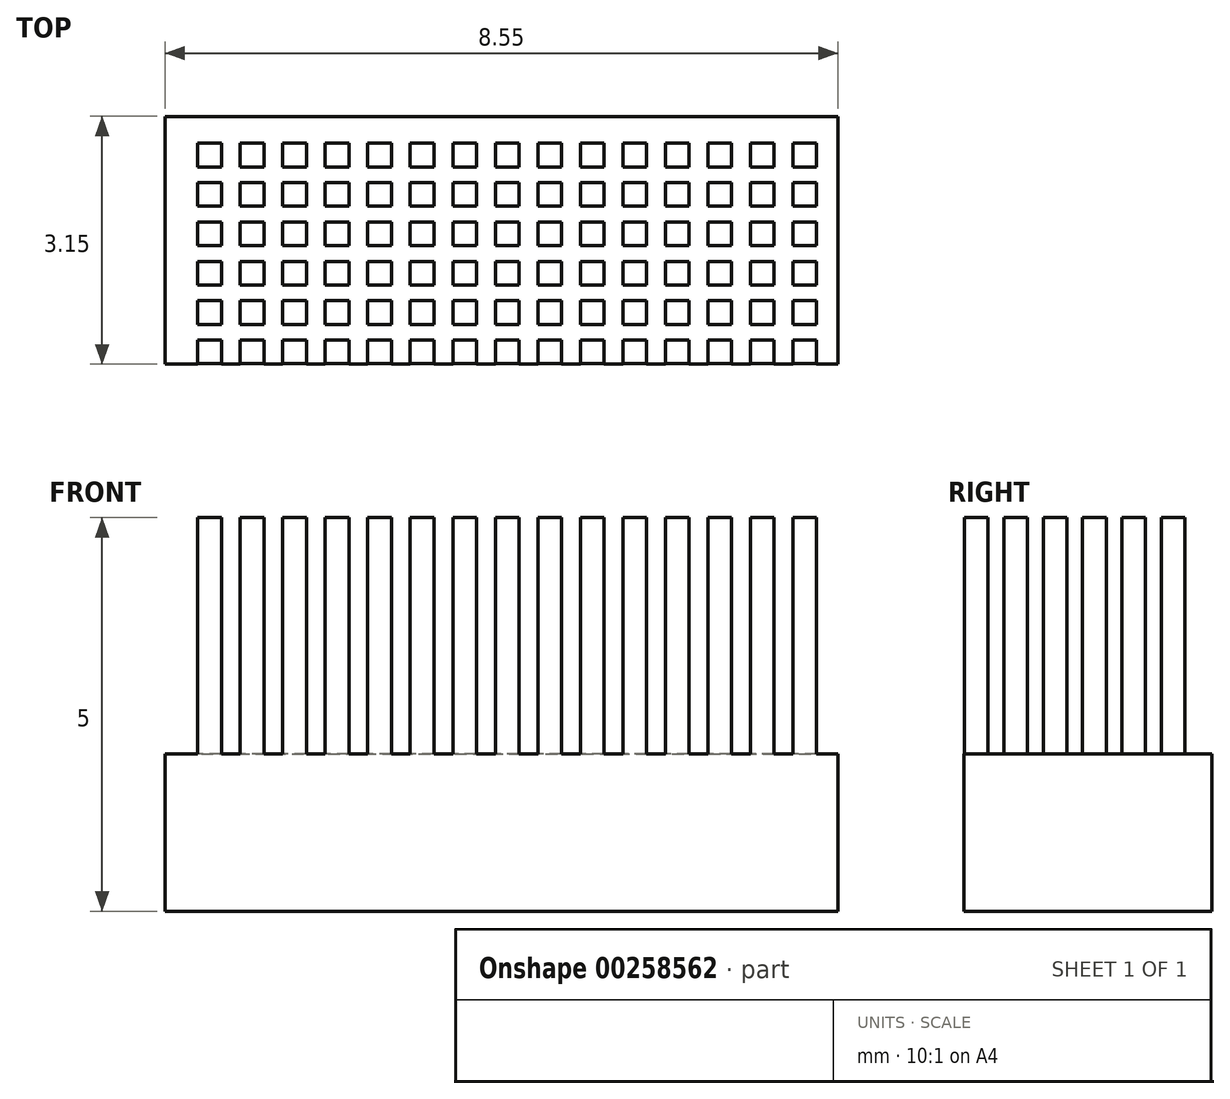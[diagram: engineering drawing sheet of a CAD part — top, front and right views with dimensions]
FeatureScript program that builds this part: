
annotation { "Feature Type Name" : "Feature", "Feature Type Description" : "" }
export const myFeature = defineFeature(function(context is Context, id is Id, definition is map)
    precondition{}
    {
        {
            var Q0;
            Q0=qCreatedBy(makeId("Top.planeOp"),FACE);
            var sketch = newSketch(context, id + "F0", { "sketchPlane" : qUnion([Q0])});
            skLineSegment(sketch, "E0.bottom", {"start": v(-12.29, 13.69) * mm, "end": v(-3.74, 13.69) * mm});
            skLineSegment(sketch, "E0.top", {"start": v(-12.29, 10.54) * mm, "end": v(-3.74, 10.54) * mm});
            skLineSegment(sketch, "E0.left", {"start": v(-12.29, 13.69) * mm, "end": v(-12.29, 10.54) * mm});
            skLineSegment(sketch, "E0.right", {"start": v(-3.74, 13.69) * mm, "end": v(-3.74, 10.54) * mm});
            skLineSegment(sketch, "E1.bottom", {"start": v(-11.87, 13.35) * mm, "end": v(-11.57, 13.35) * mm});
            skLineSegment(sketch, "E1.top", {"start": v(-11.87, 13.05) * mm, "end": v(-11.57, 13.05) * mm});
            skLineSegment(sketch, "E1.left", {"start": v(-11.87, 13.35) * mm, "end": v(-11.87, 13.05) * mm});
            skLineSegment(sketch, "E1.right", {"start": v(-11.57, 13.35) * mm, "end": v(-11.57, 13.05) * mm});
            skLineSegment(sketch, "E2.0.1.0", {"start": v(-11.87, 12.85) * mm, "end": v(-11.57, 12.85) * mm});
            skLineSegment(sketch, "E2.0.1.1", {"start": v(-11.57, 12.85) * mm, "end": v(-11.57, 12.55) * mm});
            skLineSegment(sketch, "E2.0.1.2", {"start": v(-11.87, 12.55) * mm, "end": v(-11.57, 12.55) * mm});
            skLineSegment(sketch, "E2.0.1.3", {"start": v(-11.87, 12.85) * mm, "end": v(-11.87, 12.55) * mm});
            skLineSegment(sketch, "E2.0.2.0", {"start": v(-11.87, 12.35) * mm, "end": v(-11.57, 12.35) * mm});
            skLineSegment(sketch, "E2.0.2.1", {"start": v(-11.57, 12.35) * mm, "end": v(-11.57, 12.05) * mm});
            skLineSegment(sketch, "E2.0.2.2", {"start": v(-11.87, 12.05) * mm, "end": v(-11.57, 12.05) * mm});
            skLineSegment(sketch, "E2.0.2.3", {"start": v(-11.87, 12.35) * mm, "end": v(-11.87, 12.05) * mm});
            skLineSegment(sketch, "E2.0.3.0", {"start": v(-11.87, 11.85) * mm, "end": v(-11.57, 11.85) * mm});
            skLineSegment(sketch, "E2.0.3.1", {"start": v(-11.57, 11.85) * mm, "end": v(-11.57, 11.55) * mm});
            skLineSegment(sketch, "E2.0.3.2", {"start": v(-11.87, 11.55) * mm, "end": v(-11.57, 11.55) * mm});
            skLineSegment(sketch, "E2.0.3.3", {"start": v(-11.87, 11.85) * mm, "end": v(-11.87, 11.55) * mm});
            skLineSegment(sketch, "E2.0.4.0", {"start": v(-11.87, 11.35) * mm, "end": v(-11.57, 11.35) * mm});
            skLineSegment(sketch, "E2.0.4.1", {"start": v(-11.57, 11.35) * mm, "end": v(-11.57, 11.05) * mm});
            skLineSegment(sketch, "E2.0.4.2", {"start": v(-11.87, 11.05) * mm, "end": v(-11.57, 11.05) * mm});
            skLineSegment(sketch, "E2.0.4.3", {"start": v(-11.87, 11.35) * mm, "end": v(-11.87, 11.05) * mm});
            skLineSegment(sketch, "E2.0.5.0", {"start": v(-11.87, 10.85) * mm, "end": v(-11.57, 10.85) * mm});
            skLineSegment(sketch, "E2.0.5.1", {"start": v(-11.57, 10.85) * mm, "end": v(-11.57, 10.55) * mm});
            skLineSegment(sketch, "E2.0.5.2", {"start": v(-11.87, 10.55) * mm, "end": v(-11.57, 10.55) * mm});
            skLineSegment(sketch, "E2.0.5.3", {"start": v(-11.87, 10.85) * mm, "end": v(-11.87, 10.55) * mm});
            skLineSegment(sketch, "E2.1.0.0", {"start": v(-11.33, 13.35) * mm, "end": v(-11.03, 13.35) * mm});
            skLineSegment(sketch, "E2.1.0.1", {"start": v(-11.03, 13.35) * mm, "end": v(-11.03, 13.05) * mm});
            skLineSegment(sketch, "E2.1.0.2", {"start": v(-11.33, 13.05) * mm, "end": v(-11.03, 13.05) * mm});
            skLineSegment(sketch, "E2.1.0.3", {"start": v(-11.33, 13.35) * mm, "end": v(-11.33, 13.05) * mm});
            skLineSegment(sketch, "E2.1.1.0", {"start": v(-11.33, 12.85) * mm, "end": v(-11.03, 12.85) * mm});
            skLineSegment(sketch, "E2.1.1.1", {"start": v(-11.03, 12.85) * mm, "end": v(-11.03, 12.55) * mm});
            skLineSegment(sketch, "E2.1.1.2", {"start": v(-11.33, 12.55) * mm, "end": v(-11.03, 12.55) * mm});
            skLineSegment(sketch, "E2.1.1.3", {"start": v(-11.33, 12.85) * mm, "end": v(-11.33, 12.55) * mm});
            skLineSegment(sketch, "E2.1.2.0", {"start": v(-11.33, 12.35) * mm, "end": v(-11.03, 12.35) * mm});
            skLineSegment(sketch, "E2.1.2.1", {"start": v(-11.03, 12.35) * mm, "end": v(-11.03, 12.05) * mm});
            skLineSegment(sketch, "E2.1.2.2", {"start": v(-11.33, 12.05) * mm, "end": v(-11.03, 12.05) * mm});
            skLineSegment(sketch, "E2.1.2.3", {"start": v(-11.33, 12.35) * mm, "end": v(-11.33, 12.05) * mm});
            skLineSegment(sketch, "E2.1.3.0", {"start": v(-11.33, 11.85) * mm, "end": v(-11.03, 11.85) * mm});
            skLineSegment(sketch, "E2.1.3.1", {"start": v(-11.03, 11.85) * mm, "end": v(-11.03, 11.55) * mm});
            skLineSegment(sketch, "E2.1.3.2", {"start": v(-11.33, 11.55) * mm, "end": v(-11.03, 11.55) * mm});
            skLineSegment(sketch, "E2.1.3.3", {"start": v(-11.33, 11.85) * mm, "end": v(-11.33, 11.55) * mm});
            skLineSegment(sketch, "E2.1.4.0", {"start": v(-11.33, 11.35) * mm, "end": v(-11.03, 11.35) * mm});
            skLineSegment(sketch, "E2.1.4.1", {"start": v(-11.03, 11.35) * mm, "end": v(-11.03, 11.05) * mm});
            skLineSegment(sketch, "E2.1.4.2", {"start": v(-11.33, 11.05) * mm, "end": v(-11.03, 11.05) * mm});
            skLineSegment(sketch, "E2.1.4.3", {"start": v(-11.33, 11.35) * mm, "end": v(-11.33, 11.05) * mm});
            skLineSegment(sketch, "E2.1.5.0", {"start": v(-11.33, 10.85) * mm, "end": v(-11.03, 10.85) * mm});
            skLineSegment(sketch, "E2.1.5.1", {"start": v(-11.03, 10.85) * mm, "end": v(-11.03, 10.55) * mm});
            skLineSegment(sketch, "E2.1.5.2", {"start": v(-11.33, 10.55) * mm, "end": v(-11.03, 10.55) * mm});
            skLineSegment(sketch, "E2.1.5.3", {"start": v(-11.33, 10.85) * mm, "end": v(-11.33, 10.55) * mm});
            skLineSegment(sketch, "E2.2.0.0", {"start": v(-10.8, 13.35) * mm, "end": v(-10.5, 13.35) * mm});
            skLineSegment(sketch, "E2.2.0.1", {"start": v(-10.5, 13.35) * mm, "end": v(-10.5, 13.05) * mm});
            skLineSegment(sketch, "E2.2.0.2", {"start": v(-10.8, 13.05) * mm, "end": v(-10.5, 13.05) * mm});
            skLineSegment(sketch, "E2.2.0.3", {"start": v(-10.8, 13.35) * mm, "end": v(-10.8, 13.05) * mm});
            skLineSegment(sketch, "E2.2.1.0", {"start": v(-10.8, 12.85) * mm, "end": v(-10.5, 12.85) * mm});
            skLineSegment(sketch, "E2.2.1.1", {"start": v(-10.5, 12.85) * mm, "end": v(-10.5, 12.55) * mm});
            skLineSegment(sketch, "E2.2.1.2", {"start": v(-10.8, 12.55) * mm, "end": v(-10.5, 12.55) * mm});
            skLineSegment(sketch, "E2.2.1.3", {"start": v(-10.8, 12.85) * mm, "end": v(-10.8, 12.55) * mm});
            skLineSegment(sketch, "E2.2.2.0", {"start": v(-10.8, 12.35) * mm, "end": v(-10.5, 12.35) * mm});
            skLineSegment(sketch, "E2.2.2.1", {"start": v(-10.5, 12.35) * mm, "end": v(-10.5, 12.05) * mm});
            skLineSegment(sketch, "E2.2.2.2", {"start": v(-10.8, 12.05) * mm, "end": v(-10.5, 12.05) * mm});
            skLineSegment(sketch, "E2.2.2.3", {"start": v(-10.8, 12.35) * mm, "end": v(-10.8, 12.05) * mm});
            skLineSegment(sketch, "E2.2.3.0", {"start": v(-10.8, 11.85) * mm, "end": v(-10.5, 11.85) * mm});
            skLineSegment(sketch, "E2.2.3.1", {"start": v(-10.5, 11.85) * mm, "end": v(-10.5, 11.55) * mm});
            skLineSegment(sketch, "E2.2.3.2", {"start": v(-10.8, 11.55) * mm, "end": v(-10.5, 11.55) * mm});
            skLineSegment(sketch, "E2.2.3.3", {"start": v(-10.8, 11.85) * mm, "end": v(-10.8, 11.55) * mm});
            skLineSegment(sketch, "E2.2.4.0", {"start": v(-10.8, 11.35) * mm, "end": v(-10.5, 11.35) * mm});
            skLineSegment(sketch, "E2.2.4.1", {"start": v(-10.5, 11.35) * mm, "end": v(-10.5, 11.05) * mm});
            skLineSegment(sketch, "E2.2.4.2", {"start": v(-10.8, 11.05) * mm, "end": v(-10.5, 11.05) * mm});
            skLineSegment(sketch, "E2.2.4.3", {"start": v(-10.8, 11.35) * mm, "end": v(-10.8, 11.05) * mm});
            skLineSegment(sketch, "E2.2.5.0", {"start": v(-10.8, 10.85) * mm, "end": v(-10.5, 10.85) * mm});
            skLineSegment(sketch, "E2.2.5.1", {"start": v(-10.5, 10.85) * mm, "end": v(-10.5, 10.55) * mm});
            skLineSegment(sketch, "E2.2.5.2", {"start": v(-10.8, 10.55) * mm, "end": v(-10.5, 10.55) * mm});
            skLineSegment(sketch, "E2.2.5.3", {"start": v(-10.8, 10.85) * mm, "end": v(-10.8, 10.55) * mm});
            skLineSegment(sketch, "E2.3.0.0", {"start": v(-10.25, 13.35) * mm, "end": v(-9.95, 13.35) * mm});
            skLineSegment(sketch, "E2.3.0.1", {"start": v(-9.95, 13.35) * mm, "end": v(-9.95, 13.05) * mm});
            skLineSegment(sketch, "E2.3.0.2", {"start": v(-10.25, 13.05) * mm, "end": v(-9.95, 13.05) * mm});
            skLineSegment(sketch, "E2.3.0.3", {"start": v(-10.25, 13.35) * mm, "end": v(-10.25, 13.05) * mm});
            skLineSegment(sketch, "E2.3.1.0", {"start": v(-10.25, 12.85) * mm, "end": v(-9.95, 12.85) * mm});
            skLineSegment(sketch, "E2.3.1.1", {"start": v(-9.95, 12.85) * mm, "end": v(-9.95, 12.55) * mm});
            skLineSegment(sketch, "E2.3.1.2", {"start": v(-10.25, 12.55) * mm, "end": v(-9.95, 12.55) * mm});
            skLineSegment(sketch, "E2.3.1.3", {"start": v(-10.25, 12.85) * mm, "end": v(-10.25, 12.55) * mm});
            skLineSegment(sketch, "E2.3.2.0", {"start": v(-10.25, 12.35) * mm, "end": v(-9.95, 12.35) * mm});
            skLineSegment(sketch, "E2.3.2.1", {"start": v(-9.95, 12.35) * mm, "end": v(-9.95, 12.05) * mm});
            skLineSegment(sketch, "E2.3.2.2", {"start": v(-10.25, 12.05) * mm, "end": v(-9.95, 12.05) * mm});
            skLineSegment(sketch, "E2.3.2.3", {"start": v(-10.25, 12.35) * mm, "end": v(-10.25, 12.05) * mm});
            skLineSegment(sketch, "E2.3.3.0", {"start": v(-10.25, 11.85) * mm, "end": v(-9.95, 11.85) * mm});
            skLineSegment(sketch, "E2.3.3.1", {"start": v(-9.95, 11.85) * mm, "end": v(-9.95, 11.55) * mm});
            skLineSegment(sketch, "E2.3.3.2", {"start": v(-10.25, 11.55) * mm, "end": v(-9.95, 11.55) * mm});
            skLineSegment(sketch, "E2.3.3.3", {"start": v(-10.25, 11.85) * mm, "end": v(-10.25, 11.55) * mm});
            skLineSegment(sketch, "E2.3.4.0", {"start": v(-10.25, 11.35) * mm, "end": v(-9.95, 11.35) * mm});
            skLineSegment(sketch, "E2.3.4.1", {"start": v(-9.95, 11.35) * mm, "end": v(-9.95, 11.05) * mm});
            skLineSegment(sketch, "E2.3.4.2", {"start": v(-10.25, 11.05) * mm, "end": v(-9.95, 11.05) * mm});
            skLineSegment(sketch, "E2.3.4.3", {"start": v(-10.25, 11.35) * mm, "end": v(-10.25, 11.05) * mm});
            skLineSegment(sketch, "E2.3.5.0", {"start": v(-10.25, 10.85) * mm, "end": v(-9.95, 10.85) * mm});
            skLineSegment(sketch, "E2.3.5.1", {"start": v(-9.95, 10.85) * mm, "end": v(-9.95, 10.55) * mm});
            skLineSegment(sketch, "E2.3.5.2", {"start": v(-10.25, 10.55) * mm, "end": v(-9.95, 10.55) * mm});
            skLineSegment(sketch, "E2.3.5.3", {"start": v(-10.25, 10.85) * mm, "end": v(-10.25, 10.55) * mm});
            skLineSegment(sketch, "E2.4.0.0", {"start": v(-9.71, 13.35) * mm, "end": v(-9.41, 13.35) * mm});
            skLineSegment(sketch, "E2.4.0.1", {"start": v(-9.41, 13.35) * mm, "end": v(-9.41, 13.05) * mm});
            skLineSegment(sketch, "E2.4.0.2", {"start": v(-9.71, 13.05) * mm, "end": v(-9.41, 13.05) * mm});
            skLineSegment(sketch, "E2.4.0.3", {"start": v(-9.71, 13.35) * mm, "end": v(-9.71, 13.05) * mm});
            skLineSegment(sketch, "E2.4.1.0", {"start": v(-9.71, 12.85) * mm, "end": v(-9.41, 12.85) * mm});
            skLineSegment(sketch, "E2.4.1.1", {"start": v(-9.41, 12.85) * mm, "end": v(-9.41, 12.55) * mm});
            skLineSegment(sketch, "E2.4.1.2", {"start": v(-9.71, 12.55) * mm, "end": v(-9.41, 12.55) * mm});
            skLineSegment(sketch, "E2.4.1.3", {"start": v(-9.71, 12.85) * mm, "end": v(-9.71, 12.55) * mm});
            skLineSegment(sketch, "E2.4.2.0", {"start": v(-9.71, 12.35) * mm, "end": v(-9.41, 12.35) * mm});
            skLineSegment(sketch, "E2.4.2.1", {"start": v(-9.41, 12.35) * mm, "end": v(-9.41, 12.05) * mm});
            skLineSegment(sketch, "E2.4.2.2", {"start": v(-9.71, 12.05) * mm, "end": v(-9.41, 12.05) * mm});
            skLineSegment(sketch, "E2.4.2.3", {"start": v(-9.71, 12.35) * mm, "end": v(-9.71, 12.05) * mm});
            skLineSegment(sketch, "E2.4.3.0", {"start": v(-9.71, 11.85) * mm, "end": v(-9.41, 11.85) * mm});
            skLineSegment(sketch, "E2.4.3.1", {"start": v(-9.41, 11.85) * mm, "end": v(-9.41, 11.55) * mm});
            skLineSegment(sketch, "E2.4.3.2", {"start": v(-9.71, 11.55) * mm, "end": v(-9.41, 11.55) * mm});
            skLineSegment(sketch, "E2.4.3.3", {"start": v(-9.71, 11.85) * mm, "end": v(-9.71, 11.55) * mm});
            skLineSegment(sketch, "E2.4.4.0", {"start": v(-9.71, 11.35) * mm, "end": v(-9.41, 11.35) * mm});
            skLineSegment(sketch, "E2.4.4.1", {"start": v(-9.41, 11.35) * mm, "end": v(-9.41, 11.05) * mm});
            skLineSegment(sketch, "E2.4.4.2", {"start": v(-9.71, 11.05) * mm, "end": v(-9.41, 11.05) * mm});
            skLineSegment(sketch, "E2.4.4.3", {"start": v(-9.71, 11.35) * mm, "end": v(-9.71, 11.05) * mm});
            skLineSegment(sketch, "E2.4.5.0", {"start": v(-9.71, 10.85) * mm, "end": v(-9.41, 10.85) * mm});
            skLineSegment(sketch, "E2.4.5.1", {"start": v(-9.41, 10.85) * mm, "end": v(-9.41, 10.55) * mm});
            skLineSegment(sketch, "E2.4.5.2", {"start": v(-9.71, 10.55) * mm, "end": v(-9.41, 10.55) * mm});
            skLineSegment(sketch, "E2.4.5.3", {"start": v(-9.71, 10.85) * mm, "end": v(-9.71, 10.55) * mm});
            skLineSegment(sketch, "E2.5.0.0", {"start": v(-9.17, 13.35) * mm, "end": v(-8.87, 13.35) * mm});
            skLineSegment(sketch, "E2.5.0.1", {"start": v(-8.87, 13.35) * mm, "end": v(-8.87, 13.05) * mm});
            skLineSegment(sketch, "E2.5.0.2", {"start": v(-9.17, 13.05) * mm, "end": v(-8.87, 13.05) * mm});
            skLineSegment(sketch, "E2.5.0.3", {"start": v(-9.17, 13.35) * mm, "end": v(-9.17, 13.05) * mm});
            skLineSegment(sketch, "E2.5.1.0", {"start": v(-9.17, 12.85) * mm, "end": v(-8.87, 12.85) * mm});
            skLineSegment(sketch, "E2.5.1.1", {"start": v(-8.87, 12.85) * mm, "end": v(-8.87, 12.55) * mm});
            skLineSegment(sketch, "E2.5.1.2", {"start": v(-9.17, 12.55) * mm, "end": v(-8.87, 12.55) * mm});
            skLineSegment(sketch, "E2.5.1.3", {"start": v(-9.17, 12.85) * mm, "end": v(-9.17, 12.55) * mm});
            skLineSegment(sketch, "E2.5.2.0", {"start": v(-9.17, 12.35) * mm, "end": v(-8.87, 12.35) * mm});
            skLineSegment(sketch, "E2.5.2.1", {"start": v(-8.87, 12.35) * mm, "end": v(-8.87, 12.05) * mm});
            skLineSegment(sketch, "E2.5.2.2", {"start": v(-9.17, 12.05) * mm, "end": v(-8.87, 12.05) * mm});
            skLineSegment(sketch, "E2.5.2.3", {"start": v(-9.17, 12.35) * mm, "end": v(-9.17, 12.05) * mm});
            skLineSegment(sketch, "E2.5.3.0", {"start": v(-9.17, 11.85) * mm, "end": v(-8.87, 11.85) * mm});
            skLineSegment(sketch, "E2.5.3.1", {"start": v(-8.87, 11.85) * mm, "end": v(-8.87, 11.55) * mm});
            skLineSegment(sketch, "E2.5.3.2", {"start": v(-9.17, 11.55) * mm, "end": v(-8.87, 11.55) * mm});
            skLineSegment(sketch, "E2.5.3.3", {"start": v(-9.17, 11.85) * mm, "end": v(-9.17, 11.55) * mm});
            skLineSegment(sketch, "E2.5.4.0", {"start": v(-9.17, 11.35) * mm, "end": v(-8.87, 11.35) * mm});
            skLineSegment(sketch, "E2.5.4.1", {"start": v(-8.87, 11.35) * mm, "end": v(-8.87, 11.05) * mm});
            skLineSegment(sketch, "E2.5.4.2", {"start": v(-9.17, 11.05) * mm, "end": v(-8.87, 11.05) * mm});
            skLineSegment(sketch, "E2.5.4.3", {"start": v(-9.17, 11.35) * mm, "end": v(-9.17, 11.05) * mm});
            skLineSegment(sketch, "E2.5.5.0", {"start": v(-9.17, 10.85) * mm, "end": v(-8.87, 10.85) * mm});
            skLineSegment(sketch, "E2.5.5.1", {"start": v(-8.87, 10.85) * mm, "end": v(-8.87, 10.55) * mm});
            skLineSegment(sketch, "E2.5.5.2", {"start": v(-9.17, 10.55) * mm, "end": v(-8.87, 10.55) * mm});
            skLineSegment(sketch, "E2.5.5.3", {"start": v(-9.17, 10.85) * mm, "end": v(-9.17, 10.55) * mm});
            skLineSegment(sketch, "E2.6.0.0", {"start": v(-8.63, 13.35) * mm, "end": v(-8.33, 13.35) * mm});
            skLineSegment(sketch, "E2.6.0.1", {"start": v(-8.33, 13.35) * mm, "end": v(-8.33, 13.05) * mm});
            skLineSegment(sketch, "E2.6.0.2", {"start": v(-8.63, 13.05) * mm, "end": v(-8.33, 13.05) * mm});
            skLineSegment(sketch, "E2.6.0.3", {"start": v(-8.63, 13.35) * mm, "end": v(-8.63, 13.05) * mm});
            skLineSegment(sketch, "E2.6.1.0", {"start": v(-8.63, 12.85) * mm, "end": v(-8.33, 12.85) * mm});
            skLineSegment(sketch, "E2.6.1.1", {"start": v(-8.33, 12.85) * mm, "end": v(-8.33, 12.55) * mm});
            skLineSegment(sketch, "E2.6.1.2", {"start": v(-8.63, 12.55) * mm, "end": v(-8.33, 12.55) * mm});
            skLineSegment(sketch, "E2.6.1.3", {"start": v(-8.63, 12.85) * mm, "end": v(-8.63, 12.55) * mm});
            skLineSegment(sketch, "E2.6.2.0", {"start": v(-8.63, 12.35) * mm, "end": v(-8.33, 12.35) * mm});
            skLineSegment(sketch, "E2.6.2.1", {"start": v(-8.33, 12.35) * mm, "end": v(-8.33, 12.05) * mm});
            skLineSegment(sketch, "E2.6.2.2", {"start": v(-8.63, 12.05) * mm, "end": v(-8.33, 12.05) * mm});
            skLineSegment(sketch, "E2.6.2.3", {"start": v(-8.63, 12.35) * mm, "end": v(-8.63, 12.05) * mm});
            skLineSegment(sketch, "E2.6.3.0", {"start": v(-8.63, 11.85) * mm, "end": v(-8.33, 11.85) * mm});
            skLineSegment(sketch, "E2.6.3.1", {"start": v(-8.33, 11.85) * mm, "end": v(-8.33, 11.55) * mm});
            skLineSegment(sketch, "E2.6.3.2", {"start": v(-8.63, 11.55) * mm, "end": v(-8.33, 11.55) * mm});
            skLineSegment(sketch, "E2.6.3.3", {"start": v(-8.63, 11.85) * mm, "end": v(-8.63, 11.55) * mm});
            skLineSegment(sketch, "E2.6.4.0", {"start": v(-8.63, 11.35) * mm, "end": v(-8.33, 11.35) * mm});
            skLineSegment(sketch, "E2.6.4.1", {"start": v(-8.33, 11.35) * mm, "end": v(-8.33, 11.05) * mm});
            skLineSegment(sketch, "E2.6.4.2", {"start": v(-8.63, 11.05) * mm, "end": v(-8.33, 11.05) * mm});
            skLineSegment(sketch, "E2.6.4.3", {"start": v(-8.63, 11.35) * mm, "end": v(-8.63, 11.05) * mm});
            skLineSegment(sketch, "E2.6.5.0", {"start": v(-8.63, 10.85) * mm, "end": v(-8.33, 10.85) * mm});
            skLineSegment(sketch, "E2.6.5.1", {"start": v(-8.33, 10.85) * mm, "end": v(-8.33, 10.55) * mm});
            skLineSegment(sketch, "E2.6.5.2", {"start": v(-8.63, 10.55) * mm, "end": v(-8.33, 10.55) * mm});
            skLineSegment(sketch, "E2.6.5.3", {"start": v(-8.63, 10.85) * mm, "end": v(-8.63, 10.55) * mm});
            skLineSegment(sketch, "E2.7.0.0", {"start": v(-8.1, 13.35) * mm, "end": v(-7.8, 13.35) * mm});
            skLineSegment(sketch, "E2.7.0.1", {"start": v(-7.8, 13.35) * mm, "end": v(-7.8, 13.05) * mm});
            skLineSegment(sketch, "E2.7.0.2", {"start": v(-8.1, 13.05) * mm, "end": v(-7.8, 13.05) * mm});
            skLineSegment(sketch, "E2.7.0.3", {"start": v(-8.1, 13.35) * mm, "end": v(-8.1, 13.05) * mm});
            skLineSegment(sketch, "E2.7.1.0", {"start": v(-8.1, 12.85) * mm, "end": v(-7.8, 12.85) * mm});
            skLineSegment(sketch, "E2.7.1.1", {"start": v(-7.8, 12.85) * mm, "end": v(-7.8, 12.55) * mm});
            skLineSegment(sketch, "E2.7.1.2", {"start": v(-8.1, 12.55) * mm, "end": v(-7.8, 12.55) * mm});
            skLineSegment(sketch, "E2.7.1.3", {"start": v(-8.1, 12.85) * mm, "end": v(-8.1, 12.55) * mm});
            skLineSegment(sketch, "E2.7.2.0", {"start": v(-8.1, 12.35) * mm, "end": v(-7.8, 12.35) * mm});
            skLineSegment(sketch, "E2.7.2.1", {"start": v(-7.8, 12.35) * mm, "end": v(-7.8, 12.05) * mm});
            skLineSegment(sketch, "E2.7.2.2", {"start": v(-8.1, 12.05) * mm, "end": v(-7.8, 12.05) * mm});
            skLineSegment(sketch, "E2.7.2.3", {"start": v(-8.1, 12.35) * mm, "end": v(-8.1, 12.05) * mm});
            skLineSegment(sketch, "E2.7.3.0", {"start": v(-8.1, 11.85) * mm, "end": v(-7.8, 11.85) * mm});
            skLineSegment(sketch, "E2.7.3.1", {"start": v(-7.8, 11.85) * mm, "end": v(-7.8, 11.55) * mm});
            skLineSegment(sketch, "E2.7.3.2", {"start": v(-8.1, 11.55) * mm, "end": v(-7.8, 11.55) * mm});
            skLineSegment(sketch, "E2.7.3.3", {"start": v(-8.1, 11.85) * mm, "end": v(-8.1, 11.55) * mm});
            skLineSegment(sketch, "E2.7.4.0", {"start": v(-8.1, 11.35) * mm, "end": v(-7.8, 11.35) * mm});
            skLineSegment(sketch, "E2.7.4.1", {"start": v(-7.8, 11.35) * mm, "end": v(-7.8, 11.05) * mm});
            skLineSegment(sketch, "E2.7.4.2", {"start": v(-8.1, 11.05) * mm, "end": v(-7.8, 11.05) * mm});
            skLineSegment(sketch, "E2.7.4.3", {"start": v(-8.1, 11.35) * mm, "end": v(-8.1, 11.05) * mm});
            skLineSegment(sketch, "E2.7.5.0", {"start": v(-8.1, 10.85) * mm, "end": v(-7.8, 10.85) * mm});
            skLineSegment(sketch, "E2.7.5.1", {"start": v(-7.8, 10.85) * mm, "end": v(-7.8, 10.55) * mm});
            skLineSegment(sketch, "E2.7.5.2", {"start": v(-8.1, 10.55) * mm, "end": v(-7.8, 10.55) * mm});
            skLineSegment(sketch, "E2.7.5.3", {"start": v(-8.1, 10.85) * mm, "end": v(-8.1, 10.55) * mm});
            skLineSegment(sketch, "E2.8.0.0", {"start": v(-7.55, 13.35) * mm, "end": v(-7.25, 13.35) * mm});
            skLineSegment(sketch, "E2.8.0.1", {"start": v(-7.25, 13.35) * mm, "end": v(-7.25, 13.05) * mm});
            skLineSegment(sketch, "E2.8.0.2", {"start": v(-7.55, 13.05) * mm, "end": v(-7.25, 13.05) * mm});
            skLineSegment(sketch, "E2.8.0.3", {"start": v(-7.55, 13.35) * mm, "end": v(-7.55, 13.05) * mm});
            skLineSegment(sketch, "E2.8.1.0", {"start": v(-7.55, 12.85) * mm, "end": v(-7.25, 12.85) * mm});
            skLineSegment(sketch, "E2.8.1.1", {"start": v(-7.25, 12.85) * mm, "end": v(-7.25, 12.55) * mm});
            skLineSegment(sketch, "E2.8.1.2", {"start": v(-7.55, 12.55) * mm, "end": v(-7.25, 12.55) * mm});
            skLineSegment(sketch, "E2.8.1.3", {"start": v(-7.55, 12.85) * mm, "end": v(-7.55, 12.55) * mm});
            skLineSegment(sketch, "E2.8.2.0", {"start": v(-7.55, 12.35) * mm, "end": v(-7.25, 12.35) * mm});
            skLineSegment(sketch, "E2.8.2.1", {"start": v(-7.25, 12.35) * mm, "end": v(-7.25, 12.05) * mm});
            skLineSegment(sketch, "E2.8.2.2", {"start": v(-7.55, 12.05) * mm, "end": v(-7.25, 12.05) * mm});
            skLineSegment(sketch, "E2.8.2.3", {"start": v(-7.55, 12.35) * mm, "end": v(-7.55, 12.05) * mm});
            skLineSegment(sketch, "E2.8.3.0", {"start": v(-7.55, 11.85) * mm, "end": v(-7.25, 11.85) * mm});
            skLineSegment(sketch, "E2.8.3.1", {"start": v(-7.25, 11.85) * mm, "end": v(-7.25, 11.55) * mm});
            skLineSegment(sketch, "E2.8.3.2", {"start": v(-7.55, 11.55) * mm, "end": v(-7.25, 11.55) * mm});
            skLineSegment(sketch, "E2.8.3.3", {"start": v(-7.55, 11.85) * mm, "end": v(-7.55, 11.55) * mm});
            skLineSegment(sketch, "E2.8.4.0", {"start": v(-7.55, 11.35) * mm, "end": v(-7.25, 11.35) * mm});
            skLineSegment(sketch, "E2.8.4.1", {"start": v(-7.25, 11.35) * mm, "end": v(-7.25, 11.05) * mm});
            skLineSegment(sketch, "E2.8.4.2", {"start": v(-7.55, 11.05) * mm, "end": v(-7.25, 11.05) * mm});
            skLineSegment(sketch, "E2.8.4.3", {"start": v(-7.55, 11.35) * mm, "end": v(-7.55, 11.05) * mm});
            skLineSegment(sketch, "E2.8.5.0", {"start": v(-7.55, 10.85) * mm, "end": v(-7.25, 10.85) * mm});
            skLineSegment(sketch, "E2.8.5.1", {"start": v(-7.25, 10.85) * mm, "end": v(-7.25, 10.55) * mm});
            skLineSegment(sketch, "E2.8.5.2", {"start": v(-7.55, 10.55) * mm, "end": v(-7.25, 10.55) * mm});
            skLineSegment(sketch, "E2.8.5.3", {"start": v(-7.55, 10.85) * mm, "end": v(-7.55, 10.55) * mm});
            skLineSegment(sketch, "E2.9.0.0", {"start": v(-7.01, 13.35) * mm, "end": v(-6.71, 13.35) * mm});
            skLineSegment(sketch, "E2.9.0.1", {"start": v(-6.71, 13.35) * mm, "end": v(-6.71, 13.05) * mm});
            skLineSegment(sketch, "E2.9.0.2", {"start": v(-7.01, 13.05) * mm, "end": v(-6.71, 13.05) * mm});
            skLineSegment(sketch, "E2.9.0.3", {"start": v(-7.01, 13.35) * mm, "end": v(-7.01, 13.05) * mm});
            skLineSegment(sketch, "E2.9.1.0", {"start": v(-7.01, 12.85) * mm, "end": v(-6.71, 12.85) * mm});
            skLineSegment(sketch, "E2.9.1.1", {"start": v(-6.71, 12.85) * mm, "end": v(-6.71, 12.55) * mm});
            skLineSegment(sketch, "E2.9.1.2", {"start": v(-7.01, 12.55) * mm, "end": v(-6.71, 12.55) * mm});
            skLineSegment(sketch, "E2.9.1.3", {"start": v(-7.01, 12.85) * mm, "end": v(-7.01, 12.55) * mm});
            skLineSegment(sketch, "E2.9.2.0", {"start": v(-7.01, 12.35) * mm, "end": v(-6.71, 12.35) * mm});
            skLineSegment(sketch, "E2.9.2.1", {"start": v(-6.71, 12.35) * mm, "end": v(-6.71, 12.05) * mm});
            skLineSegment(sketch, "E2.9.2.2", {"start": v(-7.01, 12.05) * mm, "end": v(-6.71, 12.05) * mm});
            skLineSegment(sketch, "E2.9.2.3", {"start": v(-7.01, 12.35) * mm, "end": v(-7.01, 12.05) * mm});
            skLineSegment(sketch, "E2.9.3.0", {"start": v(-7.01, 11.85) * mm, "end": v(-6.71, 11.85) * mm});
            skLineSegment(sketch, "E2.9.3.1", {"start": v(-6.71, 11.85) * mm, "end": v(-6.71, 11.55) * mm});
            skLineSegment(sketch, "E2.9.3.2", {"start": v(-7.01, 11.55) * mm, "end": v(-6.71, 11.55) * mm});
            skLineSegment(sketch, "E2.9.3.3", {"start": v(-7.01, 11.85) * mm, "end": v(-7.01, 11.55) * mm});
            skLineSegment(sketch, "E2.9.4.0", {"start": v(-7.01, 11.35) * mm, "end": v(-6.71, 11.35) * mm});
            skLineSegment(sketch, "E2.9.4.1", {"start": v(-6.71, 11.35) * mm, "end": v(-6.71, 11.05) * mm});
            skLineSegment(sketch, "E2.9.4.2", {"start": v(-7.01, 11.05) * mm, "end": v(-6.71, 11.05) * mm});
            skLineSegment(sketch, "E2.9.4.3", {"start": v(-7.01, 11.35) * mm, "end": v(-7.01, 11.05) * mm});
            skLineSegment(sketch, "E2.9.5.0", {"start": v(-7.01, 10.85) * mm, "end": v(-6.71, 10.85) * mm});
            skLineSegment(sketch, "E2.9.5.1", {"start": v(-6.71, 10.85) * mm, "end": v(-6.71, 10.55) * mm});
            skLineSegment(sketch, "E2.9.5.2", {"start": v(-7.01, 10.55) * mm, "end": v(-6.71, 10.55) * mm});
            skLineSegment(sketch, "E2.9.5.3", {"start": v(-7.01, 10.85) * mm, "end": v(-7.01, 10.55) * mm});
            skLineSegment(sketch, "E2.10.0.0", {"start": v(-6.47, 13.35) * mm, "end": v(-6.17, 13.35) * mm});
            skLineSegment(sketch, "E2.10.0.1", {"start": v(-6.17, 13.35) * mm, "end": v(-6.17, 13.05) * mm});
            skLineSegment(sketch, "E2.10.0.2", {"start": v(-6.47, 13.05) * mm, "end": v(-6.17, 13.05) * mm});
            skLineSegment(sketch, "E2.10.0.3", {"start": v(-6.47, 13.35) * mm, "end": v(-6.47, 13.05) * mm});
            skLineSegment(sketch, "E2.10.1.0", {"start": v(-6.47, 12.85) * mm, "end": v(-6.17, 12.85) * mm});
            skLineSegment(sketch, "E2.10.1.1", {"start": v(-6.17, 12.85) * mm, "end": v(-6.17, 12.55) * mm});
            skLineSegment(sketch, "E2.10.1.2", {"start": v(-6.47, 12.55) * mm, "end": v(-6.17, 12.55) * mm});
            skLineSegment(sketch, "E2.10.1.3", {"start": v(-6.47, 12.85) * mm, "end": v(-6.47, 12.55) * mm});
            skLineSegment(sketch, "E2.10.2.0", {"start": v(-6.47, 12.35) * mm, "end": v(-6.17, 12.35) * mm});
            skLineSegment(sketch, "E2.10.2.1", {"start": v(-6.17, 12.35) * mm, "end": v(-6.17, 12.05) * mm});
            skLineSegment(sketch, "E2.10.2.2", {"start": v(-6.47, 12.05) * mm, "end": v(-6.17, 12.05) * mm});
            skLineSegment(sketch, "E2.10.2.3", {"start": v(-6.47, 12.35) * mm, "end": v(-6.47, 12.05) * mm});
            skLineSegment(sketch, "E2.10.3.0", {"start": v(-6.47, 11.85) * mm, "end": v(-6.17, 11.85) * mm});
            skLineSegment(sketch, "E2.10.3.1", {"start": v(-6.17, 11.85) * mm, "end": v(-6.17, 11.55) * mm});
            skLineSegment(sketch, "E2.10.3.2", {"start": v(-6.47, 11.55) * mm, "end": v(-6.17, 11.55) * mm});
            skLineSegment(sketch, "E2.10.3.3", {"start": v(-6.47, 11.85) * mm, "end": v(-6.47, 11.55) * mm});
            skLineSegment(sketch, "E2.10.4.0", {"start": v(-6.47, 11.35) * mm, "end": v(-6.17, 11.35) * mm});
            skLineSegment(sketch, "E2.10.4.1", {"start": v(-6.17, 11.35) * mm, "end": v(-6.17, 11.05) * mm});
            skLineSegment(sketch, "E2.10.4.2", {"start": v(-6.47, 11.05) * mm, "end": v(-6.17, 11.05) * mm});
            skLineSegment(sketch, "E2.10.4.3", {"start": v(-6.47, 11.35) * mm, "end": v(-6.47, 11.05) * mm});
            skLineSegment(sketch, "E2.10.5.0", {"start": v(-6.47, 10.85) * mm, "end": v(-6.17, 10.85) * mm});
            skLineSegment(sketch, "E2.10.5.1", {"start": v(-6.17, 10.85) * mm, "end": v(-6.17, 10.55) * mm});
            skLineSegment(sketch, "E2.10.5.2", {"start": v(-6.47, 10.55) * mm, "end": v(-6.17, 10.55) * mm});
            skLineSegment(sketch, "E2.10.5.3", {"start": v(-6.47, 10.85) * mm, "end": v(-6.47, 10.55) * mm});
            skLineSegment(sketch, "E2.11.0.0", {"start": v(-5.93, 13.35) * mm, "end": v(-5.63, 13.35) * mm});
            skLineSegment(sketch, "E2.11.0.1", {"start": v(-5.63, 13.35) * mm, "end": v(-5.63, 13.05) * mm});
            skLineSegment(sketch, "E2.11.0.2", {"start": v(-5.93, 13.05) * mm, "end": v(-5.63, 13.05) * mm});
            skLineSegment(sketch, "E2.11.0.3", {"start": v(-5.93, 13.35) * mm, "end": v(-5.93, 13.05) * mm});
            skLineSegment(sketch, "E2.11.1.0", {"start": v(-5.93, 12.85) * mm, "end": v(-5.63, 12.85) * mm});
            skLineSegment(sketch, "E2.11.1.1", {"start": v(-5.63, 12.85) * mm, "end": v(-5.63, 12.55) * mm});
            skLineSegment(sketch, "E2.11.1.2", {"start": v(-5.93, 12.55) * mm, "end": v(-5.63, 12.55) * mm});
            skLineSegment(sketch, "E2.11.1.3", {"start": v(-5.93, 12.85) * mm, "end": v(-5.93, 12.55) * mm});
            skLineSegment(sketch, "E2.11.2.0", {"start": v(-5.93, 12.35) * mm, "end": v(-5.63, 12.35) * mm});
            skLineSegment(sketch, "E2.11.2.1", {"start": v(-5.63, 12.35) * mm, "end": v(-5.63, 12.05) * mm});
            skLineSegment(sketch, "E2.11.2.2", {"start": v(-5.93, 12.05) * mm, "end": v(-5.63, 12.05) * mm});
            skLineSegment(sketch, "E2.11.2.3", {"start": v(-5.93, 12.35) * mm, "end": v(-5.93, 12.05) * mm});
            skLineSegment(sketch, "E2.11.3.0", {"start": v(-5.93, 11.85) * mm, "end": v(-5.63, 11.85) * mm});
            skLineSegment(sketch, "E2.11.3.1", {"start": v(-5.63, 11.85) * mm, "end": v(-5.63, 11.55) * mm});
            skLineSegment(sketch, "E2.11.3.2", {"start": v(-5.93, 11.55) * mm, "end": v(-5.63, 11.55) * mm});
            skLineSegment(sketch, "E2.11.3.3", {"start": v(-5.93, 11.85) * mm, "end": v(-5.93, 11.55) * mm});
            skLineSegment(sketch, "E2.11.4.0", {"start": v(-5.93, 11.35) * mm, "end": v(-5.63, 11.35) * mm});
            skLineSegment(sketch, "E2.11.4.1", {"start": v(-5.63, 11.35) * mm, "end": v(-5.63, 11.05) * mm});
            skLineSegment(sketch, "E2.11.4.2", {"start": v(-5.93, 11.05) * mm, "end": v(-5.63, 11.05) * mm});
            skLineSegment(sketch, "E2.11.4.3", {"start": v(-5.93, 11.35) * mm, "end": v(-5.93, 11.05) * mm});
            skLineSegment(sketch, "E2.11.5.0", {"start": v(-5.93, 10.85) * mm, "end": v(-5.63, 10.85) * mm});
            skLineSegment(sketch, "E2.11.5.1", {"start": v(-5.63, 10.85) * mm, "end": v(-5.63, 10.55) * mm});
            skLineSegment(sketch, "E2.11.5.2", {"start": v(-5.93, 10.55) * mm, "end": v(-5.63, 10.55) * mm});
            skLineSegment(sketch, "E2.11.5.3", {"start": v(-5.93, 10.85) * mm, "end": v(-5.93, 10.55) * mm});
            skLineSegment(sketch, "E2.12.0.0", {"start": v(-5.4, 13.35) * mm, "end": v(-5.1, 13.35) * mm});
            skLineSegment(sketch, "E2.12.0.1", {"start": v(-5.1, 13.35) * mm, "end": v(-5.1, 13.05) * mm});
            skLineSegment(sketch, "E2.12.0.2", {"start": v(-5.4, 13.05) * mm, "end": v(-5.1, 13.05) * mm});
            skLineSegment(sketch, "E2.12.0.3", {"start": v(-5.4, 13.35) * mm, "end": v(-5.4, 13.05) * mm});
            skLineSegment(sketch, "E2.12.1.0", {"start": v(-5.4, 12.85) * mm, "end": v(-5.1, 12.85) * mm});
            skLineSegment(sketch, "E2.12.1.1", {"start": v(-5.1, 12.85) * mm, "end": v(-5.1, 12.55) * mm});
            skLineSegment(sketch, "E2.12.1.2", {"start": v(-5.4, 12.55) * mm, "end": v(-5.1, 12.55) * mm});
            skLineSegment(sketch, "E2.12.1.3", {"start": v(-5.4, 12.85) * mm, "end": v(-5.4, 12.55) * mm});
            skLineSegment(sketch, "E2.12.2.0", {"start": v(-5.4, 12.35) * mm, "end": v(-5.1, 12.35) * mm});
            skLineSegment(sketch, "E2.12.2.1", {"start": v(-5.1, 12.35) * mm, "end": v(-5.1, 12.05) * mm});
            skLineSegment(sketch, "E2.12.2.2", {"start": v(-5.4, 12.05) * mm, "end": v(-5.1, 12.05) * mm});
            skLineSegment(sketch, "E2.12.2.3", {"start": v(-5.4, 12.35) * mm, "end": v(-5.4, 12.05) * mm});
            skLineSegment(sketch, "E2.12.3.0", {"start": v(-5.4, 11.85) * mm, "end": v(-5.1, 11.85) * mm});
            skLineSegment(sketch, "E2.12.3.1", {"start": v(-5.1, 11.85) * mm, "end": v(-5.1, 11.55) * mm});
            skLineSegment(sketch, "E2.12.3.2", {"start": v(-5.4, 11.55) * mm, "end": v(-5.1, 11.55) * mm});
            skLineSegment(sketch, "E2.12.3.3", {"start": v(-5.4, 11.85) * mm, "end": v(-5.4, 11.55) * mm});
            skLineSegment(sketch, "E2.12.4.0", {"start": v(-5.4, 11.35) * mm, "end": v(-5.1, 11.35) * mm});
            skLineSegment(sketch, "E2.12.4.1", {"start": v(-5.1, 11.35) * mm, "end": v(-5.1, 11.05) * mm});
            skLineSegment(sketch, "E2.12.4.2", {"start": v(-5.4, 11.05) * mm, "end": v(-5.1, 11.05) * mm});
            skLineSegment(sketch, "E2.12.4.3", {"start": v(-5.4, 11.35) * mm, "end": v(-5.4, 11.05) * mm});
            skLineSegment(sketch, "E2.12.5.0", {"start": v(-5.4, 10.85) * mm, "end": v(-5.1, 10.85) * mm});
            skLineSegment(sketch, "E2.12.5.1", {"start": v(-5.1, 10.85) * mm, "end": v(-5.1, 10.55) * mm});
            skLineSegment(sketch, "E2.12.5.2", {"start": v(-5.4, 10.55) * mm, "end": v(-5.1, 10.55) * mm});
            skLineSegment(sketch, "E2.12.5.3", {"start": v(-5.4, 10.85) * mm, "end": v(-5.4, 10.55) * mm});
            skLineSegment(sketch, "E2.13.0.0", {"start": v(-4.85, 13.35) * mm, "end": v(-4.55, 13.35) * mm});
            skLineSegment(sketch, "E2.13.0.1", {"start": v(-4.55, 13.35) * mm, "end": v(-4.55, 13.05) * mm});
            skLineSegment(sketch, "E2.13.0.2", {"start": v(-4.85, 13.05) * mm, "end": v(-4.55, 13.05) * mm});
            skLineSegment(sketch, "E2.13.0.3", {"start": v(-4.85, 13.35) * mm, "end": v(-4.85, 13.05) * mm});
            skLineSegment(sketch, "E2.13.1.0", {"start": v(-4.85, 12.85) * mm, "end": v(-4.55, 12.85) * mm});
            skLineSegment(sketch, "E2.13.1.1", {"start": v(-4.55, 12.85) * mm, "end": v(-4.55, 12.55) * mm});
            skLineSegment(sketch, "E2.13.1.2", {"start": v(-4.85, 12.55) * mm, "end": v(-4.55, 12.55) * mm});
            skLineSegment(sketch, "E2.13.1.3", {"start": v(-4.85, 12.85) * mm, "end": v(-4.85, 12.55) * mm});
            skLineSegment(sketch, "E2.13.2.0", {"start": v(-4.85, 12.35) * mm, "end": v(-4.55, 12.35) * mm});
            skLineSegment(sketch, "E2.13.2.1", {"start": v(-4.55, 12.35) * mm, "end": v(-4.55, 12.05) * mm});
            skLineSegment(sketch, "E2.13.2.2", {"start": v(-4.85, 12.05) * mm, "end": v(-4.55, 12.05) * mm});
            skLineSegment(sketch, "E2.13.2.3", {"start": v(-4.85, 12.35) * mm, "end": v(-4.85, 12.05) * mm});
            skLineSegment(sketch, "E2.13.3.0", {"start": v(-4.85, 11.85) * mm, "end": v(-4.55, 11.85) * mm});
            skLineSegment(sketch, "E2.13.3.1", {"start": v(-4.55, 11.85) * mm, "end": v(-4.55, 11.55) * mm});
            skLineSegment(sketch, "E2.13.3.2", {"start": v(-4.85, 11.55) * mm, "end": v(-4.55, 11.55) * mm});
            skLineSegment(sketch, "E2.13.3.3", {"start": v(-4.85, 11.85) * mm, "end": v(-4.85, 11.55) * mm});
            skLineSegment(sketch, "E2.13.4.0", {"start": v(-4.85, 11.35) * mm, "end": v(-4.55, 11.35) * mm});
            skLineSegment(sketch, "E2.13.4.1", {"start": v(-4.55, 11.35) * mm, "end": v(-4.55, 11.05) * mm});
            skLineSegment(sketch, "E2.13.4.2", {"start": v(-4.85, 11.05) * mm, "end": v(-4.55, 11.05) * mm});
            skLineSegment(sketch, "E2.13.4.3", {"start": v(-4.85, 11.35) * mm, "end": v(-4.85, 11.05) * mm});
            skLineSegment(sketch, "E2.13.5.0", {"start": v(-4.85, 10.85) * mm, "end": v(-4.55, 10.85) * mm});
            skLineSegment(sketch, "E2.13.5.1", {"start": v(-4.55, 10.85) * mm, "end": v(-4.55, 10.55) * mm});
            skLineSegment(sketch, "E2.13.5.2", {"start": v(-4.85, 10.55) * mm, "end": v(-4.55, 10.55) * mm});
            skLineSegment(sketch, "E2.13.5.3", {"start": v(-4.85, 10.85) * mm, "end": v(-4.85, 10.55) * mm});
            skLineSegment(sketch, "E2.14.0.0", {"start": v(-4.31, 13.35) * mm, "end": v(-4.01, 13.35) * mm});
            skLineSegment(sketch, "E2.14.0.1", {"start": v(-4.01, 13.35) * mm, "end": v(-4.01, 13.05) * mm});
            skLineSegment(sketch, "E2.14.0.2", {"start": v(-4.31, 13.05) * mm, "end": v(-4.01, 13.05) * mm});
            skLineSegment(sketch, "E2.14.0.3", {"start": v(-4.31, 13.35) * mm, "end": v(-4.31, 13.05) * mm});
            skLineSegment(sketch, "E2.14.1.0", {"start": v(-4.31, 12.85) * mm, "end": v(-4.01, 12.85) * mm});
            skLineSegment(sketch, "E2.14.1.1", {"start": v(-4.01, 12.85) * mm, "end": v(-4.01, 12.55) * mm});
            skLineSegment(sketch, "E2.14.1.2", {"start": v(-4.31, 12.55) * mm, "end": v(-4.01, 12.55) * mm});
            skLineSegment(sketch, "E2.14.1.3", {"start": v(-4.31, 12.85) * mm, "end": v(-4.31, 12.55) * mm});
            skLineSegment(sketch, "E2.14.2.0", {"start": v(-4.31, 12.35) * mm, "end": v(-4.01, 12.35) * mm});
            skLineSegment(sketch, "E2.14.2.1", {"start": v(-4.01, 12.35) * mm, "end": v(-4.01, 12.05) * mm});
            skLineSegment(sketch, "E2.14.2.2", {"start": v(-4.31, 12.05) * mm, "end": v(-4.01, 12.05) * mm});
            skLineSegment(sketch, "E2.14.2.3", {"start": v(-4.31, 12.35) * mm, "end": v(-4.31, 12.05) * mm});
            skLineSegment(sketch, "E2.14.3.0", {"start": v(-4.31, 11.85) * mm, "end": v(-4.01, 11.85) * mm});
            skLineSegment(sketch, "E2.14.3.1", {"start": v(-4.01, 11.85) * mm, "end": v(-4.01, 11.55) * mm});
            skLineSegment(sketch, "E2.14.3.2", {"start": v(-4.31, 11.55) * mm, "end": v(-4.01, 11.55) * mm});
            skLineSegment(sketch, "E2.14.3.3", {"start": v(-4.31, 11.85) * mm, "end": v(-4.31, 11.55) * mm});
            skLineSegment(sketch, "E2.14.4.0", {"start": v(-4.31, 11.35) * mm, "end": v(-4.01, 11.35) * mm});
            skLineSegment(sketch, "E2.14.4.1", {"start": v(-4.01, 11.35) * mm, "end": v(-4.01, 11.05) * mm});
            skLineSegment(sketch, "E2.14.4.2", {"start": v(-4.31, 11.05) * mm, "end": v(-4.01, 11.05) * mm});
            skLineSegment(sketch, "E2.14.4.3", {"start": v(-4.31, 11.35) * mm, "end": v(-4.31, 11.05) * mm});
            skLineSegment(sketch, "E2.14.5.0", {"start": v(-4.31, 10.85) * mm, "end": v(-4.01, 10.85) * mm});
            skLineSegment(sketch, "E2.14.5.1", {"start": v(-4.01, 10.85) * mm, "end": v(-4.01, 10.55) * mm});
            skLineSegment(sketch, "E2.14.5.2", {"start": v(-4.31, 10.55) * mm, "end": v(-4.01, 10.55) * mm});
            skLineSegment(sketch, "E2.14.5.3", {"start": v(-4.31, 10.85) * mm, "end": v(-4.31, 10.55) * mm});
            skLineSegment(sketch, "E2.direction1", {"start": v(-11.87, 13.35) * mm, "end": v(-11.33, 13.35) * mm, "construction": true});
            skLineSegment(sketch, "E2.direction2", {"start": v(-11.87, 13.35) * mm, "end": v(-11.87, 12.85) * mm, "construction": true});
            skSolve(sketch);
        }
        {
            var Q0;
            Q0=makeQuery(id+"F0.imprint","IMPRINT",FACE,{"disambiguationData":[TD([[makeQuery(id+"F0.imprint","IMPRINT",EDGE,{"derivedFrom":sQuery(id+"F0.wireOp",EDGE,"E0.bottom")}),-1.0]])]});
            var Q1;
            Q1=makeQuery(id+"F0.imprint","IMPRINT",FACE,{"disambiguationData":[TD([[makeQuery(id+"F0.imprint","IMPRINT",EDGE,{"derivedFrom":sQuery(id+"F0.wireOp",EDGE,"E1.bottom")}),-1.0]])]});
            var Q2;
            Q2=makeQuery(id+"F0.imprint","IMPRINT",FACE,{"disambiguationData":[TD([[makeQuery(id+"F0.imprint","IMPRINT",EDGE,{"derivedFrom":sQuery(id+"F0.wireOp",EDGE,"E2.0.1.0")}),-1.0]])]});
            var Q3;
            Q3=makeQuery(id+"F0.imprint","IMPRINT",FACE,{"disambiguationData":[TD([[makeQuery(id+"F0.imprint","IMPRINT",EDGE,{"derivedFrom":sQuery(id+"F0.wireOp",EDGE,"E2.0.2.0")}),-1.0]])]});
            var Q4;
            Q4=makeQuery(id+"F0.imprint","IMPRINT",FACE,{"disambiguationData":[TD([[makeQuery(id+"F0.imprint","IMPRINT",EDGE,{"derivedFrom":sQuery(id+"F0.wireOp",EDGE,"E2.0.3.0")}),-1.0]])]});
            var Q5;
            Q5=makeQuery(id+"F0.imprint","IMPRINT",FACE,{"disambiguationData":[TD([[makeQuery(id+"F0.imprint","IMPRINT",EDGE,{"derivedFrom":sQuery(id+"F0.wireOp",EDGE,"E2.0.4.0")}),-1.0]])]});
            var Q6;
            Q6=makeQuery(id+"F0.imprint","IMPRINT",FACE,{"disambiguationData":[TD([[makeQuery(id+"F0.imprint","IMPRINT",EDGE,{"derivedFrom":sQuery(id+"F0.wireOp",EDGE,"E2.0.5.0")}),-1.0]])]});
            var Q7;
            Q7=makeQuery(id+"F0.imprint","IMPRINT",FACE,{"disambiguationData":[TD([[makeQuery(id+"F0.imprint","IMPRINT",EDGE,{"derivedFrom":sQuery(id+"F0.wireOp",EDGE,"E2.1.0.0")}),-1.0]])]});
            var Q8;
            Q8=makeQuery(id+"F0.imprint","IMPRINT",FACE,{"disambiguationData":[TD([[makeQuery(id+"F0.imprint","IMPRINT",EDGE,{"derivedFrom":sQuery(id+"F0.wireOp",EDGE,"E2.1.1.0")}),-1.0]])]});
            var Q9;
            Q9=makeQuery(id+"F0.imprint","IMPRINT",FACE,{"disambiguationData":[TD([[makeQuery(id+"F0.imprint","IMPRINT",EDGE,{"derivedFrom":sQuery(id+"F0.wireOp",EDGE,"E2.1.2.0")}),-1.0]])]});
            var Q10;
            Q10=makeQuery(id+"F0.imprint","IMPRINT",FACE,{"disambiguationData":[TD([[makeQuery(id+"F0.imprint","IMPRINT",EDGE,{"derivedFrom":sQuery(id+"F0.wireOp",EDGE,"E2.1.3.0")}),-1.0]])]});
            var Q11;
            Q11=makeQuery(id+"F0.imprint","IMPRINT",FACE,{"disambiguationData":[TD([[makeQuery(id+"F0.imprint","IMPRINT",EDGE,{"derivedFrom":sQuery(id+"F0.wireOp",EDGE,"E2.1.4.0")}),-1.0]])]});
            var Q12;
            Q12=makeQuery(id+"F0.imprint","IMPRINT",FACE,{"disambiguationData":[TD([[makeQuery(id+"F0.imprint","IMPRINT",EDGE,{"derivedFrom":sQuery(id+"F0.wireOp",EDGE,"E2.1.5.0")}),-1.0]])]});
            var Q13;
            Q13=makeQuery(id+"F0.imprint","IMPRINT",FACE,{"disambiguationData":[TD([[makeQuery(id+"F0.imprint","IMPRINT",EDGE,{"derivedFrom":sQuery(id+"F0.wireOp",EDGE,"E2.2.0.0")}),-1.0]])]});
            var Q14;
            Q14=makeQuery(id+"F0.imprint","IMPRINT",FACE,{"disambiguationData":[TD([[makeQuery(id+"F0.imprint","IMPRINT",EDGE,{"derivedFrom":sQuery(id+"F0.wireOp",EDGE,"E2.2.1.0")}),-1.0]])]});
            var Q15;
            Q15=makeQuery(id+"F0.imprint","IMPRINT",FACE,{"disambiguationData":[TD([[makeQuery(id+"F0.imprint","IMPRINT",EDGE,{"derivedFrom":sQuery(id+"F0.wireOp",EDGE,"E2.2.2.0")}),-1.0]])]});
            var Q16;
            Q16=makeQuery(id+"F0.imprint","IMPRINT",FACE,{"disambiguationData":[TD([[makeQuery(id+"F0.imprint","IMPRINT",EDGE,{"derivedFrom":sQuery(id+"F0.wireOp",EDGE,"E2.2.3.0")}),-1.0]])]});
            var Q17;
            Q17=makeQuery(id+"F0.imprint","IMPRINT",FACE,{"disambiguationData":[TD([[makeQuery(id+"F0.imprint","IMPRINT",EDGE,{"derivedFrom":sQuery(id+"F0.wireOp",EDGE,"E2.2.4.0")}),-1.0]])]});
            var Q18;
            Q18=makeQuery(id+"F0.imprint","IMPRINT",FACE,{"disambiguationData":[TD([[makeQuery(id+"F0.imprint","IMPRINT",EDGE,{"derivedFrom":sQuery(id+"F0.wireOp",EDGE,"E2.2.5.0")}),-1.0]])]});
            var Q19;
            Q19=makeQuery(id+"F0.imprint","IMPRINT",FACE,{"disambiguationData":[TD([[makeQuery(id+"F0.imprint","IMPRINT",EDGE,{"derivedFrom":sQuery(id+"F0.wireOp",EDGE,"E2.3.0.0")}),-1.0]])]});
            var Q20;
            Q20=makeQuery(id+"F0.imprint","IMPRINT",FACE,{"disambiguationData":[TD([[makeQuery(id+"F0.imprint","IMPRINT",EDGE,{"derivedFrom":sQuery(id+"F0.wireOp",EDGE,"E2.3.1.0")}),-1.0]])]});
            var Q21;
            Q21=makeQuery(id+"F0.imprint","IMPRINT",FACE,{"disambiguationData":[TD([[makeQuery(id+"F0.imprint","IMPRINT",EDGE,{"derivedFrom":sQuery(id+"F0.wireOp",EDGE,"E2.3.2.0")}),-1.0]])]});
            var Q22;
            Q22=makeQuery(id+"F0.imprint","IMPRINT",FACE,{"disambiguationData":[TD([[makeQuery(id+"F0.imprint","IMPRINT",EDGE,{"derivedFrom":sQuery(id+"F0.wireOp",EDGE,"E2.3.3.0")}),-1.0]])]});
            var Q23;
            Q23=makeQuery(id+"F0.imprint","IMPRINT",FACE,{"disambiguationData":[TD([[makeQuery(id+"F0.imprint","IMPRINT",EDGE,{"derivedFrom":sQuery(id+"F0.wireOp",EDGE,"E2.3.4.0")}),-1.0]])]});
            var Q24;
            Q24=makeQuery(id+"F0.imprint","IMPRINT",FACE,{"disambiguationData":[TD([[makeQuery(id+"F0.imprint","IMPRINT",EDGE,{"derivedFrom":sQuery(id+"F0.wireOp",EDGE,"E2.3.5.0")}),-1.0]])]});
            var Q25;
            Q25=makeQuery(id+"F0.imprint","IMPRINT",FACE,{"disambiguationData":[TD([[makeQuery(id+"F0.imprint","IMPRINT",EDGE,{"derivedFrom":sQuery(id+"F0.wireOp",EDGE,"E2.4.0.0")}),-1.0]])]});
            var Q26;
            Q26=makeQuery(id+"F0.imprint","IMPRINT",FACE,{"disambiguationData":[TD([[makeQuery(id+"F0.imprint","IMPRINT",EDGE,{"derivedFrom":sQuery(id+"F0.wireOp",EDGE,"E2.4.1.0")}),-1.0]])]});
            var Q27;
            Q27=makeQuery(id+"F0.imprint","IMPRINT",FACE,{"disambiguationData":[TD([[makeQuery(id+"F0.imprint","IMPRINT",EDGE,{"derivedFrom":sQuery(id+"F0.wireOp",EDGE,"E2.4.2.0")}),-1.0]])]});
            var Q28;
            Q28=makeQuery(id+"F0.imprint","IMPRINT",FACE,{"disambiguationData":[TD([[makeQuery(id+"F0.imprint","IMPRINT",EDGE,{"derivedFrom":sQuery(id+"F0.wireOp",EDGE,"E2.4.3.0")}),-1.0]])]});
            var Q29;
            Q29=makeQuery(id+"F0.imprint","IMPRINT",FACE,{"disambiguationData":[TD([[makeQuery(id+"F0.imprint","IMPRINT",EDGE,{"derivedFrom":sQuery(id+"F0.wireOp",EDGE,"E2.4.4.0")}),-1.0]])]});
            var Q30;
            Q30=makeQuery(id+"F0.imprint","IMPRINT",FACE,{"disambiguationData":[TD([[makeQuery(id+"F0.imprint","IMPRINT",EDGE,{"derivedFrom":sQuery(id+"F0.wireOp",EDGE,"E2.4.5.0")}),-1.0]])]});
            var Q31;
            Q31=makeQuery(id+"F0.imprint","IMPRINT",FACE,{"disambiguationData":[TD([[makeQuery(id+"F0.imprint","IMPRINT",EDGE,{"derivedFrom":sQuery(id+"F0.wireOp",EDGE,"E2.5.0.0")}),-1.0]])]});
            var Q32;
            Q32=makeQuery(id+"F0.imprint","IMPRINT",FACE,{"disambiguationData":[TD([[makeQuery(id+"F0.imprint","IMPRINT",EDGE,{"derivedFrom":sQuery(id+"F0.wireOp",EDGE,"E2.5.1.0")}),-1.0]])]});
            var Q33;
            Q33=makeQuery(id+"F0.imprint","IMPRINT",FACE,{"disambiguationData":[TD([[makeQuery(id+"F0.imprint","IMPRINT",EDGE,{"derivedFrom":sQuery(id+"F0.wireOp",EDGE,"E2.5.2.0")}),-1.0]])]});
            var Q34;
            Q34=makeQuery(id+"F0.imprint","IMPRINT",FACE,{"disambiguationData":[TD([[makeQuery(id+"F0.imprint","IMPRINT",EDGE,{"derivedFrom":sQuery(id+"F0.wireOp",EDGE,"E2.5.3.0")}),-1.0]])]});
            var Q35;
            Q35=makeQuery(id+"F0.imprint","IMPRINT",FACE,{"disambiguationData":[TD([[makeQuery(id+"F0.imprint","IMPRINT",EDGE,{"derivedFrom":sQuery(id+"F0.wireOp",EDGE,"E2.5.4.0")}),-1.0]])]});
            var Q36;
            Q36=makeQuery(id+"F0.imprint","IMPRINT",FACE,{"disambiguationData":[TD([[makeQuery(id+"F0.imprint","IMPRINT",EDGE,{"derivedFrom":sQuery(id+"F0.wireOp",EDGE,"E2.5.5.0")}),-1.0]])]});
            var Q37;
            Q37=makeQuery(id+"F0.imprint","IMPRINT",FACE,{"disambiguationData":[TD([[makeQuery(id+"F0.imprint","IMPRINT",EDGE,{"derivedFrom":sQuery(id+"F0.wireOp",EDGE,"E2.6.0.0")}),-1.0]])]});
            var Q38;
            Q38=makeQuery(id+"F0.imprint","IMPRINT",FACE,{"disambiguationData":[TD([[makeQuery(id+"F0.imprint","IMPRINT",EDGE,{"derivedFrom":sQuery(id+"F0.wireOp",EDGE,"E2.6.1.0")}),-1.0]])]});
            var Q39;
            Q39=makeQuery(id+"F0.imprint","IMPRINT",FACE,{"disambiguationData":[TD([[makeQuery(id+"F0.imprint","IMPRINT",EDGE,{"derivedFrom":sQuery(id+"F0.wireOp",EDGE,"E2.6.2.0")}),-1.0]])]});
            var Q40;
            Q40=makeQuery(id+"F0.imprint","IMPRINT",FACE,{"disambiguationData":[TD([[makeQuery(id+"F0.imprint","IMPRINT",EDGE,{"derivedFrom":sQuery(id+"F0.wireOp",EDGE,"E2.6.3.0")}),-1.0]])]});
            var Q41;
            Q41=makeQuery(id+"F0.imprint","IMPRINT",FACE,{"disambiguationData":[TD([[makeQuery(id+"F0.imprint","IMPRINT",EDGE,{"derivedFrom":sQuery(id+"F0.wireOp",EDGE,"E2.6.4.0")}),-1.0]])]});
            var Q42;
            Q42=makeQuery(id+"F0.imprint","IMPRINT",FACE,{"disambiguationData":[TD([[makeQuery(id+"F0.imprint","IMPRINT",EDGE,{"derivedFrom":sQuery(id+"F0.wireOp",EDGE,"E2.6.5.0")}),-1.0]])]});
            var Q43;
            Q43=makeQuery(id+"F0.imprint","IMPRINT",FACE,{"disambiguationData":[TD([[makeQuery(id+"F0.imprint","IMPRINT",EDGE,{"derivedFrom":sQuery(id+"F0.wireOp",EDGE,"E2.7.0.0")}),-1.0]])]});
            var Q44;
            Q44=makeQuery(id+"F0.imprint","IMPRINT",FACE,{"disambiguationData":[TD([[makeQuery(id+"F0.imprint","IMPRINT",EDGE,{"derivedFrom":sQuery(id+"F0.wireOp",EDGE,"E2.7.1.0")}),-1.0]])]});
            var Q45;
            Q45=makeQuery(id+"F0.imprint","IMPRINT",FACE,{"disambiguationData":[TD([[makeQuery(id+"F0.imprint","IMPRINT",EDGE,{"derivedFrom":sQuery(id+"F0.wireOp",EDGE,"E2.7.2.0")}),-1.0]])]});
            var Q46;
            Q46=makeQuery(id+"F0.imprint","IMPRINT",FACE,{"disambiguationData":[TD([[makeQuery(id+"F0.imprint","IMPRINT",EDGE,{"derivedFrom":sQuery(id+"F0.wireOp",EDGE,"E2.7.3.0")}),-1.0]])]});
            var Q47;
            Q47=makeQuery(id+"F0.imprint","IMPRINT",FACE,{"disambiguationData":[TD([[makeQuery(id+"F0.imprint","IMPRINT",EDGE,{"derivedFrom":sQuery(id+"F0.wireOp",EDGE,"E2.7.4.0")}),-1.0]])]});
            var Q48;
            Q48=makeQuery(id+"F0.imprint","IMPRINT",FACE,{"disambiguationData":[TD([[makeQuery(id+"F0.imprint","IMPRINT",EDGE,{"derivedFrom":sQuery(id+"F0.wireOp",EDGE,"E2.7.5.0")}),-1.0]])]});
            var Q49;
            Q49=makeQuery(id+"F0.imprint","IMPRINT",FACE,{"disambiguationData":[TD([[makeQuery(id+"F0.imprint","IMPRINT",EDGE,{"derivedFrom":sQuery(id+"F0.wireOp",EDGE,"E2.8.0.0")}),-1.0]])]});
            var Q50;
            Q50=makeQuery(id+"F0.imprint","IMPRINT",FACE,{"disambiguationData":[TD([[makeQuery(id+"F0.imprint","IMPRINT",EDGE,{"derivedFrom":sQuery(id+"F0.wireOp",EDGE,"E2.8.1.0")}),-1.0]])]});
            var Q51;
            Q51=makeQuery(id+"F0.imprint","IMPRINT",FACE,{"disambiguationData":[TD([[makeQuery(id+"F0.imprint","IMPRINT",EDGE,{"derivedFrom":sQuery(id+"F0.wireOp",EDGE,"E2.8.2.0")}),-1.0]])]});
            var Q52;
            Q52=makeQuery(id+"F0.imprint","IMPRINT",FACE,{"disambiguationData":[TD([[makeQuery(id+"F0.imprint","IMPRINT",EDGE,{"derivedFrom":sQuery(id+"F0.wireOp",EDGE,"E2.8.3.0")}),-1.0]])]});
            var Q53;
            Q53=makeQuery(id+"F0.imprint","IMPRINT",FACE,{"disambiguationData":[TD([[makeQuery(id+"F0.imprint","IMPRINT",EDGE,{"derivedFrom":sQuery(id+"F0.wireOp",EDGE,"E2.8.4.0")}),-1.0]])]});
            var Q54;
            Q54=makeQuery(id+"F0.imprint","IMPRINT",FACE,{"disambiguationData":[TD([[makeQuery(id+"F0.imprint","IMPRINT",EDGE,{"derivedFrom":sQuery(id+"F0.wireOp",EDGE,"E2.8.5.0")}),-1.0]])]});
            var Q55;
            Q55=makeQuery(id+"F0.imprint","IMPRINT",FACE,{"disambiguationData":[TD([[makeQuery(id+"F0.imprint","IMPRINT",EDGE,{"derivedFrom":sQuery(id+"F0.wireOp",EDGE,"E2.9.0.0")}),-1.0]])]});
            var Q56;
            Q56=makeQuery(id+"F0.imprint","IMPRINT",FACE,{"disambiguationData":[TD([[makeQuery(id+"F0.imprint","IMPRINT",EDGE,{"derivedFrom":sQuery(id+"F0.wireOp",EDGE,"E2.9.1.0")}),-1.0]])]});
            var Q57;
            Q57=makeQuery(id+"F0.imprint","IMPRINT",FACE,{"disambiguationData":[TD([[makeQuery(id+"F0.imprint","IMPRINT",EDGE,{"derivedFrom":sQuery(id+"F0.wireOp",EDGE,"E2.9.2.0")}),-1.0]])]});
            var Q58;
            Q58=makeQuery(id+"F0.imprint","IMPRINT",FACE,{"disambiguationData":[TD([[makeQuery(id+"F0.imprint","IMPRINT",EDGE,{"derivedFrom":sQuery(id+"F0.wireOp",EDGE,"E2.9.3.0")}),-1.0]])]});
            var Q59;
            Q59=makeQuery(id+"F0.imprint","IMPRINT",FACE,{"disambiguationData":[TD([[makeQuery(id+"F0.imprint","IMPRINT",EDGE,{"derivedFrom":sQuery(id+"F0.wireOp",EDGE,"E2.9.4.0")}),-1.0]])]});
            var Q60;
            Q60=makeQuery(id+"F0.imprint","IMPRINT",FACE,{"disambiguationData":[TD([[makeQuery(id+"F0.imprint","IMPRINT",EDGE,{"derivedFrom":sQuery(id+"F0.wireOp",EDGE,"E2.9.5.0")}),-1.0]])]});
            var Q61;
            Q61=makeQuery(id+"F0.imprint","IMPRINT",FACE,{"disambiguationData":[TD([[makeQuery(id+"F0.imprint","IMPRINT",EDGE,{"derivedFrom":sQuery(id+"F0.wireOp",EDGE,"E2.10.0.0")}),-1.0]])]});
            var Q62;
            Q62=makeQuery(id+"F0.imprint","IMPRINT",FACE,{"disambiguationData":[TD([[makeQuery(id+"F0.imprint","IMPRINT",EDGE,{"derivedFrom":sQuery(id+"F0.wireOp",EDGE,"E2.10.1.0")}),-1.0]])]});
            var Q63;
            Q63=makeQuery(id+"F0.imprint","IMPRINT",FACE,{"disambiguationData":[TD([[makeQuery(id+"F0.imprint","IMPRINT",EDGE,{"derivedFrom":sQuery(id+"F0.wireOp",EDGE,"E2.10.2.0")}),-1.0]])]});
            var Q64;
            Q64=makeQuery(id+"F0.imprint","IMPRINT",FACE,{"disambiguationData":[TD([[makeQuery(id+"F0.imprint","IMPRINT",EDGE,{"derivedFrom":sQuery(id+"F0.wireOp",EDGE,"E2.10.3.0")}),-1.0]])]});
            var Q65;
            Q65=makeQuery(id+"F0.imprint","IMPRINT",FACE,{"disambiguationData":[TD([[makeQuery(id+"F0.imprint","IMPRINT",EDGE,{"derivedFrom":sQuery(id+"F0.wireOp",EDGE,"E2.10.4.0")}),-1.0]])]});
            var Q66;
            Q66=makeQuery(id+"F0.imprint","IMPRINT",FACE,{"disambiguationData":[TD([[makeQuery(id+"F0.imprint","IMPRINT",EDGE,{"derivedFrom":sQuery(id+"F0.wireOp",EDGE,"E2.10.5.0")}),-1.0]])]});
            var Q67;
            Q67=makeQuery(id+"F0.imprint","IMPRINT",FACE,{"disambiguationData":[TD([[makeQuery(id+"F0.imprint","IMPRINT",EDGE,{"derivedFrom":sQuery(id+"F0.wireOp",EDGE,"E2.11.0.0")}),-1.0]])]});
            var Q68;
            Q68=makeQuery(id+"F0.imprint","IMPRINT",FACE,{"disambiguationData":[TD([[makeQuery(id+"F0.imprint","IMPRINT",EDGE,{"derivedFrom":sQuery(id+"F0.wireOp",EDGE,"E2.11.1.0")}),-1.0]])]});
            var Q69;
            Q69=makeQuery(id+"F0.imprint","IMPRINT",FACE,{"disambiguationData":[TD([[makeQuery(id+"F0.imprint","IMPRINT",EDGE,{"derivedFrom":sQuery(id+"F0.wireOp",EDGE,"E2.11.2.0")}),-1.0]])]});
            var Q70;
            Q70=makeQuery(id+"F0.imprint","IMPRINT",FACE,{"disambiguationData":[TD([[makeQuery(id+"F0.imprint","IMPRINT",EDGE,{"derivedFrom":sQuery(id+"F0.wireOp",EDGE,"E2.11.3.0")}),-1.0]])]});
            var Q71;
            Q71=makeQuery(id+"F0.imprint","IMPRINT",FACE,{"disambiguationData":[TD([[makeQuery(id+"F0.imprint","IMPRINT",EDGE,{"derivedFrom":sQuery(id+"F0.wireOp",EDGE,"E2.11.4.0")}),-1.0]])]});
            var Q72;
            Q72=makeQuery(id+"F0.imprint","IMPRINT",FACE,{"disambiguationData":[TD([[makeQuery(id+"F0.imprint","IMPRINT",EDGE,{"derivedFrom":sQuery(id+"F0.wireOp",EDGE,"E2.11.5.0")}),-1.0]])]});
            var Q73;
            Q73=makeQuery(id+"F0.imprint","IMPRINT",FACE,{"disambiguationData":[TD([[makeQuery(id+"F0.imprint","IMPRINT",EDGE,{"derivedFrom":sQuery(id+"F0.wireOp",EDGE,"E2.12.0.0")}),-1.0]])]});
            var Q74;
            Q74=makeQuery(id+"F0.imprint","IMPRINT",FACE,{"disambiguationData":[TD([[makeQuery(id+"F0.imprint","IMPRINT",EDGE,{"derivedFrom":sQuery(id+"F0.wireOp",EDGE,"E2.12.1.0")}),-1.0]])]});
            var Q75;
            Q75=makeQuery(id+"F0.imprint","IMPRINT",FACE,{"disambiguationData":[TD([[makeQuery(id+"F0.imprint","IMPRINT",EDGE,{"derivedFrom":sQuery(id+"F0.wireOp",EDGE,"E2.12.2.0")}),-1.0]])]});
            var Q76;
            Q76=makeQuery(id+"F0.imprint","IMPRINT",FACE,{"disambiguationData":[TD([[makeQuery(id+"F0.imprint","IMPRINT",EDGE,{"derivedFrom":sQuery(id+"F0.wireOp",EDGE,"E2.12.3.0")}),-1.0]])]});
            var Q77;
            Q77=makeQuery(id+"F0.imprint","IMPRINT",FACE,{"disambiguationData":[TD([[makeQuery(id+"F0.imprint","IMPRINT",EDGE,{"derivedFrom":sQuery(id+"F0.wireOp",EDGE,"E2.12.4.0")}),-1.0]])]});
            var Q78;
            Q78=makeQuery(id+"F0.imprint","IMPRINT",FACE,{"disambiguationData":[TD([[makeQuery(id+"F0.imprint","IMPRINT",EDGE,{"derivedFrom":sQuery(id+"F0.wireOp",EDGE,"E2.12.5.0")}),-1.0]])]});
            var Q79;
            Q79=makeQuery(id+"F0.imprint","IMPRINT",FACE,{"disambiguationData":[TD([[makeQuery(id+"F0.imprint","IMPRINT",EDGE,{"derivedFrom":sQuery(id+"F0.wireOp",EDGE,"E2.13.0.0")}),-1.0]])]});
            var Q80;
            Q80=makeQuery(id+"F0.imprint","IMPRINT",FACE,{"disambiguationData":[TD([[makeQuery(id+"F0.imprint","IMPRINT",EDGE,{"derivedFrom":sQuery(id+"F0.wireOp",EDGE,"E2.13.1.0")}),-1.0]])]});
            var Q81;
            Q81=makeQuery(id+"F0.imprint","IMPRINT",FACE,{"disambiguationData":[TD([[makeQuery(id+"F0.imprint","IMPRINT",EDGE,{"derivedFrom":sQuery(id+"F0.wireOp",EDGE,"E2.13.2.0")}),-1.0]])]});
            var Q82;
            Q82=makeQuery(id+"F0.imprint","IMPRINT",FACE,{"disambiguationData":[TD([[makeQuery(id+"F0.imprint","IMPRINT",EDGE,{"derivedFrom":sQuery(id+"F0.wireOp",EDGE,"E2.13.3.0")}),-1.0]])]});
            var Q83;
            Q83=makeQuery(id+"F0.imprint","IMPRINT",FACE,{"disambiguationData":[TD([[makeQuery(id+"F0.imprint","IMPRINT",EDGE,{"derivedFrom":sQuery(id+"F0.wireOp",EDGE,"E2.13.4.0")}),-1.0]])]});
            var Q84;
            Q84=makeQuery(id+"F0.imprint","IMPRINT",FACE,{"disambiguationData":[TD([[makeQuery(id+"F0.imprint","IMPRINT",EDGE,{"derivedFrom":sQuery(id+"F0.wireOp",EDGE,"E2.13.5.0")}),-1.0]])]});
            var Q85;
            Q85=makeQuery(id+"F0.imprint","IMPRINT",FACE,{"disambiguationData":[TD([[makeQuery(id+"F0.imprint","IMPRINT",EDGE,{"derivedFrom":sQuery(id+"F0.wireOp",EDGE,"E2.14.0.0")}),-1.0]])]});
            var Q86;
            Q86=makeQuery(id+"F0.imprint","IMPRINT",FACE,{"disambiguationData":[TD([[makeQuery(id+"F0.imprint","IMPRINT",EDGE,{"derivedFrom":sQuery(id+"F0.wireOp",EDGE,"E2.14.1.0")}),-1.0]])]});
            var Q87;
            Q87=makeQuery(id+"F0.imprint","IMPRINT",FACE,{"disambiguationData":[TD([[makeQuery(id+"F0.imprint","IMPRINT",EDGE,{"derivedFrom":sQuery(id+"F0.wireOp",EDGE,"E2.14.2.0")}),-1.0]])]});
            var Q88;
            Q88=makeQuery(id+"F0.imprint","IMPRINT",FACE,{"disambiguationData":[TD([[makeQuery(id+"F0.imprint","IMPRINT",EDGE,{"derivedFrom":sQuery(id+"F0.wireOp",EDGE,"E2.14.3.0")}),-1.0]])]});
            var Q89;
            Q89=makeQuery(id+"F0.imprint","IMPRINT",FACE,{"disambiguationData":[TD([[makeQuery(id+"F0.imprint","IMPRINT",EDGE,{"derivedFrom":sQuery(id+"F0.wireOp",EDGE,"E2.14.4.0")}),-1.0]])]});
            var Q90;
            Q90=makeQuery(id+"F0.imprint","IMPRINT",FACE,{"disambiguationData":[TD([[makeQuery(id+"F0.imprint","IMPRINT",EDGE,{"derivedFrom":sQuery(id+"F0.wireOp",EDGE,"E2.14.5.0")}),-1.0]])]});
            extrude(context, id + "F1", {"entities" : qUnion([Q0, Q1, Q2, Q3, Q4, Q5, Q6, Q7, Q8, Q9, Q10, Q11, Q12, Q13, Q14, Q15, Q16, Q17, Q18, Q19, Q20, Q21, Q22, Q23, Q24, Q25, Q26, Q27, Q28, Q29, Q30, Q31, Q32, Q33, Q34, Q35, Q36, Q37, Q38, Q39, Q40, Q41, Q42, Q43, Q44, Q45, Q46, Q47, Q48, Q49, Q50, Q51, Q52, Q53, Q54, Q55, Q56, Q57, Q58, Q59, Q60, Q61, Q62, Q63, Q64, Q65, Q66, Q67, Q68, Q69, Q70, Q71, Q72, Q73, Q74, Q75, Q76, Q77, Q78, Q79, Q80, Q81, Q82, Q83, Q84, Q85, Q86, Q87, Q88, Q89, Q90]), "depth" : 2 * mm});
        }
        {
            var Q0;
            Q0=makeQuery(id+"F0.imprint","IMPRINT",FACE,{"disambiguationData":[TD([[makeQuery(id+"F0.imprint","IMPRINT",EDGE,{"derivedFrom":sQuery(id+"F0.wireOp",EDGE,"E1.bottom")}),-1.0]])]});
            var Q1;
            Q1=makeQuery(id+"F0.imprint","IMPRINT",FACE,{"disambiguationData":[TD([[makeQuery(id+"F0.imprint","IMPRINT",EDGE,{"derivedFrom":sQuery(id+"F0.wireOp",EDGE,"E2.0.1.0")}),-1.0]])]});
            var Q2;
            Q2=makeQuery(id+"F0.imprint","IMPRINT",FACE,{"disambiguationData":[TD([[makeQuery(id+"F0.imprint","IMPRINT",EDGE,{"derivedFrom":sQuery(id+"F0.wireOp",EDGE,"E2.0.2.0")}),-1.0]])]});
            var Q3;
            Q3=makeQuery(id+"F0.imprint","IMPRINT",FACE,{"disambiguationData":[TD([[makeQuery(id+"F0.imprint","IMPRINT",EDGE,{"derivedFrom":sQuery(id+"F0.wireOp",EDGE,"E2.0.3.0")}),-1.0]])]});
            var Q4;
            Q4=makeQuery(id+"F0.imprint","IMPRINT",FACE,{"disambiguationData":[TD([[makeQuery(id+"F0.imprint","IMPRINT",EDGE,{"derivedFrom":sQuery(id+"F0.wireOp",EDGE,"E2.0.4.0")}),-1.0]])]});
            var Q5;
            Q5=makeQuery(id+"F0.imprint","IMPRINT",FACE,{"disambiguationData":[TD([[makeQuery(id+"F0.imprint","IMPRINT",EDGE,{"derivedFrom":sQuery(id+"F0.wireOp",EDGE,"E2.0.5.0")}),-1.0]])]});
            var Q6;
            Q6=makeQuery(id+"F0.imprint","IMPRINT",FACE,{"disambiguationData":[TD([[makeQuery(id+"F0.imprint","IMPRINT",EDGE,{"derivedFrom":sQuery(id+"F0.wireOp",EDGE,"E2.1.0.0")}),-1.0]])]});
            var Q7;
            Q7=makeQuery(id+"F0.imprint","IMPRINT",FACE,{"disambiguationData":[TD([[makeQuery(id+"F0.imprint","IMPRINT",EDGE,{"derivedFrom":sQuery(id+"F0.wireOp",EDGE,"E2.1.1.0")}),-1.0]])]});
            var Q8;
            Q8=makeQuery(id+"F0.imprint","IMPRINT",FACE,{"disambiguationData":[TD([[makeQuery(id+"F0.imprint","IMPRINT",EDGE,{"derivedFrom":sQuery(id+"F0.wireOp",EDGE,"E2.1.2.0")}),-1.0]])]});
            var Q9;
            Q9=makeQuery(id+"F0.imprint","IMPRINT",FACE,{"disambiguationData":[TD([[makeQuery(id+"F0.imprint","IMPRINT",EDGE,{"derivedFrom":sQuery(id+"F0.wireOp",EDGE,"E2.1.3.0")}),-1.0]])]});
            var Q10;
            Q10=makeQuery(id+"F0.imprint","IMPRINT",FACE,{"disambiguationData":[TD([[makeQuery(id+"F0.imprint","IMPRINT",EDGE,{"derivedFrom":sQuery(id+"F0.wireOp",EDGE,"E2.1.4.0")}),-1.0]])]});
            var Q11;
            Q11=makeQuery(id+"F0.imprint","IMPRINT",FACE,{"disambiguationData":[TD([[makeQuery(id+"F0.imprint","IMPRINT",EDGE,{"derivedFrom":sQuery(id+"F0.wireOp",EDGE,"E2.1.5.0")}),-1.0]])]});
            var Q12;
            Q12=makeQuery(id+"F0.imprint","IMPRINT",FACE,{"disambiguationData":[TD([[makeQuery(id+"F0.imprint","IMPRINT",EDGE,{"derivedFrom":sQuery(id+"F0.wireOp",EDGE,"E2.2.0.0")}),-1.0]])]});
            var Q13;
            Q13=makeQuery(id+"F0.imprint","IMPRINT",FACE,{"disambiguationData":[TD([[makeQuery(id+"F0.imprint","IMPRINT",EDGE,{"derivedFrom":sQuery(id+"F0.wireOp",EDGE,"E2.2.1.0")}),-1.0]])]});
            var Q14;
            Q14=makeQuery(id+"F0.imprint","IMPRINT",FACE,{"disambiguationData":[TD([[makeQuery(id+"F0.imprint","IMPRINT",EDGE,{"derivedFrom":sQuery(id+"F0.wireOp",EDGE,"E2.2.2.0")}),-1.0]])]});
            var Q15;
            Q15=makeQuery(id+"F0.imprint","IMPRINT",FACE,{"disambiguationData":[TD([[makeQuery(id+"F0.imprint","IMPRINT",EDGE,{"derivedFrom":sQuery(id+"F0.wireOp",EDGE,"E2.2.3.0")}),-1.0]])]});
            var Q16;
            Q16=makeQuery(id+"F0.imprint","IMPRINT",FACE,{"disambiguationData":[TD([[makeQuery(id+"F0.imprint","IMPRINT",EDGE,{"derivedFrom":sQuery(id+"F0.wireOp",EDGE,"E2.2.4.0")}),-1.0]])]});
            var Q17;
            Q17=makeQuery(id+"F0.imprint","IMPRINT",FACE,{"disambiguationData":[TD([[makeQuery(id+"F0.imprint","IMPRINT",EDGE,{"derivedFrom":sQuery(id+"F0.wireOp",EDGE,"E2.2.5.0")}),-1.0]])]});
            var Q18;
            Q18=makeQuery(id+"F0.imprint","IMPRINT",FACE,{"disambiguationData":[TD([[makeQuery(id+"F0.imprint","IMPRINT",EDGE,{"derivedFrom":sQuery(id+"F0.wireOp",EDGE,"E2.3.0.0")}),-1.0]])]});
            var Q19;
            Q19=makeQuery(id+"F0.imprint","IMPRINT",FACE,{"disambiguationData":[TD([[makeQuery(id+"F0.imprint","IMPRINT",EDGE,{"derivedFrom":sQuery(id+"F0.wireOp",EDGE,"E2.3.1.0")}),-1.0]])]});
            var Q20;
            Q20=makeQuery(id+"F0.imprint","IMPRINT",FACE,{"disambiguationData":[TD([[makeQuery(id+"F0.imprint","IMPRINT",EDGE,{"derivedFrom":sQuery(id+"F0.wireOp",EDGE,"E2.3.2.0")}),-1.0]])]});
            var Q21;
            Q21=makeQuery(id+"F0.imprint","IMPRINT",FACE,{"disambiguationData":[TD([[makeQuery(id+"F0.imprint","IMPRINT",EDGE,{"derivedFrom":sQuery(id+"F0.wireOp",EDGE,"E2.3.3.0")}),-1.0]])]});
            var Q22;
            Q22=makeQuery(id+"F0.imprint","IMPRINT",FACE,{"disambiguationData":[TD([[makeQuery(id+"F0.imprint","IMPRINT",EDGE,{"derivedFrom":sQuery(id+"F0.wireOp",EDGE,"E2.3.4.0")}),-1.0]])]});
            var Q23;
            Q23=makeQuery(id+"F0.imprint","IMPRINT",FACE,{"disambiguationData":[TD([[makeQuery(id+"F0.imprint","IMPRINT",EDGE,{"derivedFrom":sQuery(id+"F0.wireOp",EDGE,"E2.3.5.0")}),-1.0]])]});
            var Q24;
            Q24=makeQuery(id+"F0.imprint","IMPRINT",FACE,{"disambiguationData":[TD([[makeQuery(id+"F0.imprint","IMPRINT",EDGE,{"derivedFrom":sQuery(id+"F0.wireOp",EDGE,"E2.4.0.0")}),-1.0]])]});
            var Q25;
            Q25=makeQuery(id+"F0.imprint","IMPRINT",FACE,{"disambiguationData":[TD([[makeQuery(id+"F0.imprint","IMPRINT",EDGE,{"derivedFrom":sQuery(id+"F0.wireOp",EDGE,"E2.4.1.0")}),-1.0]])]});
            var Q26;
            Q26=makeQuery(id+"F0.imprint","IMPRINT",FACE,{"disambiguationData":[TD([[makeQuery(id+"F0.imprint","IMPRINT",EDGE,{"derivedFrom":sQuery(id+"F0.wireOp",EDGE,"E2.4.2.0")}),-1.0]])]});
            var Q27;
            Q27=makeQuery(id+"F0.imprint","IMPRINT",FACE,{"disambiguationData":[TD([[makeQuery(id+"F0.imprint","IMPRINT",EDGE,{"derivedFrom":sQuery(id+"F0.wireOp",EDGE,"E2.4.3.0")}),-1.0]])]});
            var Q28;
            Q28=makeQuery(id+"F0.imprint","IMPRINT",FACE,{"disambiguationData":[TD([[makeQuery(id+"F0.imprint","IMPRINT",EDGE,{"derivedFrom":sQuery(id+"F0.wireOp",EDGE,"E2.4.4.0")}),-1.0]])]});
            var Q29;
            Q29=makeQuery(id+"F0.imprint","IMPRINT",FACE,{"disambiguationData":[TD([[makeQuery(id+"F0.imprint","IMPRINT",EDGE,{"derivedFrom":sQuery(id+"F0.wireOp",EDGE,"E2.4.5.0")}),-1.0]])]});
            var Q30;
            Q30=makeQuery(id+"F0.imprint","IMPRINT",FACE,{"disambiguationData":[TD([[makeQuery(id+"F0.imprint","IMPRINT",EDGE,{"derivedFrom":sQuery(id+"F0.wireOp",EDGE,"E2.5.0.0")}),-1.0]])]});
            var Q31;
            Q31=makeQuery(id+"F0.imprint","IMPRINT",FACE,{"disambiguationData":[TD([[makeQuery(id+"F0.imprint","IMPRINT",EDGE,{"derivedFrom":sQuery(id+"F0.wireOp",EDGE,"E2.5.1.0")}),-1.0]])]});
            var Q32;
            Q32=makeQuery(id+"F0.imprint","IMPRINT",FACE,{"disambiguationData":[TD([[makeQuery(id+"F0.imprint","IMPRINT",EDGE,{"derivedFrom":sQuery(id+"F0.wireOp",EDGE,"E2.5.2.0")}),-1.0]])]});
            var Q33;
            Q33=makeQuery(id+"F0.imprint","IMPRINT",FACE,{"disambiguationData":[TD([[makeQuery(id+"F0.imprint","IMPRINT",EDGE,{"derivedFrom":sQuery(id+"F0.wireOp",EDGE,"E2.5.3.0")}),-1.0]])]});
            var Q34;
            Q34=makeQuery(id+"F0.imprint","IMPRINT",FACE,{"disambiguationData":[TD([[makeQuery(id+"F0.imprint","IMPRINT",EDGE,{"derivedFrom":sQuery(id+"F0.wireOp",EDGE,"E2.5.4.0")}),-1.0]])]});
            var Q35;
            Q35=makeQuery(id+"F0.imprint","IMPRINT",FACE,{"disambiguationData":[TD([[makeQuery(id+"F0.imprint","IMPRINT",EDGE,{"derivedFrom":sQuery(id+"F0.wireOp",EDGE,"E2.5.5.0")}),-1.0]])]});
            var Q36;
            Q36=makeQuery(id+"F0.imprint","IMPRINT",FACE,{"disambiguationData":[TD([[makeQuery(id+"F0.imprint","IMPRINT",EDGE,{"derivedFrom":sQuery(id+"F0.wireOp",EDGE,"E2.6.0.0")}),-1.0]])]});
            var Q37;
            Q37=makeQuery(id+"F0.imprint","IMPRINT",FACE,{"disambiguationData":[TD([[makeQuery(id+"F0.imprint","IMPRINT",EDGE,{"derivedFrom":sQuery(id+"F0.wireOp",EDGE,"E2.6.1.0")}),-1.0]])]});
            var Q38;
            Q38=makeQuery(id+"F0.imprint","IMPRINT",FACE,{"disambiguationData":[TD([[makeQuery(id+"F0.imprint","IMPRINT",EDGE,{"derivedFrom":sQuery(id+"F0.wireOp",EDGE,"E2.6.2.0")}),-1.0]])]});
            var Q39;
            Q39=makeQuery(id+"F0.imprint","IMPRINT",FACE,{"disambiguationData":[TD([[makeQuery(id+"F0.imprint","IMPRINT",EDGE,{"derivedFrom":sQuery(id+"F0.wireOp",EDGE,"E2.6.3.0")}),-1.0]])]});
            var Q40;
            Q40=makeQuery(id+"F0.imprint","IMPRINT",FACE,{"disambiguationData":[TD([[makeQuery(id+"F0.imprint","IMPRINT",EDGE,{"derivedFrom":sQuery(id+"F0.wireOp",EDGE,"E2.6.4.0")}),-1.0]])]});
            var Q41;
            Q41=makeQuery(id+"F0.imprint","IMPRINT",FACE,{"disambiguationData":[TD([[makeQuery(id+"F0.imprint","IMPRINT",EDGE,{"derivedFrom":sQuery(id+"F0.wireOp",EDGE,"E2.6.5.0")}),-1.0]])]});
            var Q42;
            Q42=makeQuery(id+"F0.imprint","IMPRINT",FACE,{"disambiguationData":[TD([[makeQuery(id+"F0.imprint","IMPRINT",EDGE,{"derivedFrom":sQuery(id+"F0.wireOp",EDGE,"E2.7.0.0")}),-1.0]])]});
            var Q43;
            Q43=makeQuery(id+"F0.imprint","IMPRINT",FACE,{"disambiguationData":[TD([[makeQuery(id+"F0.imprint","IMPRINT",EDGE,{"derivedFrom":sQuery(id+"F0.wireOp",EDGE,"E2.7.1.0")}),-1.0]])]});
            var Q44;
            Q44=makeQuery(id+"F0.imprint","IMPRINT",FACE,{"disambiguationData":[TD([[makeQuery(id+"F0.imprint","IMPRINT",EDGE,{"derivedFrom":sQuery(id+"F0.wireOp",EDGE,"E2.7.2.0")}),-1.0]])]});
            var Q45;
            Q45=makeQuery(id+"F0.imprint","IMPRINT",FACE,{"disambiguationData":[TD([[makeQuery(id+"F0.imprint","IMPRINT",EDGE,{"derivedFrom":sQuery(id+"F0.wireOp",EDGE,"E2.7.3.0")}),-1.0]])]});
            var Q46;
            Q46=makeQuery(id+"F0.imprint","IMPRINT",FACE,{"disambiguationData":[TD([[makeQuery(id+"F0.imprint","IMPRINT",EDGE,{"derivedFrom":sQuery(id+"F0.wireOp",EDGE,"E2.7.4.0")}),-1.0]])]});
            var Q47;
            Q47=makeQuery(id+"F0.imprint","IMPRINT",FACE,{"disambiguationData":[TD([[makeQuery(id+"F0.imprint","IMPRINT",EDGE,{"derivedFrom":sQuery(id+"F0.wireOp",EDGE,"E2.7.5.0")}),-1.0]])]});
            var Q48;
            Q48=makeQuery(id+"F0.imprint","IMPRINT",FACE,{"disambiguationData":[TD([[makeQuery(id+"F0.imprint","IMPRINT",EDGE,{"derivedFrom":sQuery(id+"F0.wireOp",EDGE,"E2.8.0.0")}),-1.0]])]});
            var Q49;
            Q49=makeQuery(id+"F0.imprint","IMPRINT",FACE,{"disambiguationData":[TD([[makeQuery(id+"F0.imprint","IMPRINT",EDGE,{"derivedFrom":sQuery(id+"F0.wireOp",EDGE,"E2.8.1.0")}),-1.0]])]});
            var Q50;
            Q50=makeQuery(id+"F0.imprint","IMPRINT",FACE,{"disambiguationData":[TD([[makeQuery(id+"F0.imprint","IMPRINT",EDGE,{"derivedFrom":sQuery(id+"F0.wireOp",EDGE,"E2.8.2.0")}),-1.0]])]});
            var Q51;
            Q51=makeQuery(id+"F0.imprint","IMPRINT",FACE,{"disambiguationData":[TD([[makeQuery(id+"F0.imprint","IMPRINT",EDGE,{"derivedFrom":sQuery(id+"F0.wireOp",EDGE,"E2.8.3.0")}),-1.0]])]});
            var Q52;
            Q52=makeQuery(id+"F0.imprint","IMPRINT",FACE,{"disambiguationData":[TD([[makeQuery(id+"F0.imprint","IMPRINT",EDGE,{"derivedFrom":sQuery(id+"F0.wireOp",EDGE,"E2.8.4.0")}),-1.0]])]});
            var Q53;
            Q53=makeQuery(id+"F0.imprint","IMPRINT",FACE,{"disambiguationData":[TD([[makeQuery(id+"F0.imprint","IMPRINT",EDGE,{"derivedFrom":sQuery(id+"F0.wireOp",EDGE,"E2.8.5.0")}),-1.0]])]});
            var Q54;
            Q54=makeQuery(id+"F0.imprint","IMPRINT",FACE,{"disambiguationData":[TD([[makeQuery(id+"F0.imprint","IMPRINT",EDGE,{"derivedFrom":sQuery(id+"F0.wireOp",EDGE,"E2.9.0.0")}),-1.0]])]});
            var Q55;
            Q55=makeQuery(id+"F0.imprint","IMPRINT",FACE,{"disambiguationData":[TD([[makeQuery(id+"F0.imprint","IMPRINT",EDGE,{"derivedFrom":sQuery(id+"F0.wireOp",EDGE,"E2.9.1.0")}),-1.0]])]});
            var Q56;
            Q56=makeQuery(id+"F0.imprint","IMPRINT",FACE,{"disambiguationData":[TD([[makeQuery(id+"F0.imprint","IMPRINT",EDGE,{"derivedFrom":sQuery(id+"F0.wireOp",EDGE,"E2.9.2.0")}),-1.0]])]});
            var Q57;
            Q57=makeQuery(id+"F0.imprint","IMPRINT",FACE,{"disambiguationData":[TD([[makeQuery(id+"F0.imprint","IMPRINT",EDGE,{"derivedFrom":sQuery(id+"F0.wireOp",EDGE,"E2.9.3.0")}),-1.0]])]});
            var Q58;
            Q58=makeQuery(id+"F0.imprint","IMPRINT",FACE,{"disambiguationData":[TD([[makeQuery(id+"F0.imprint","IMPRINT",EDGE,{"derivedFrom":sQuery(id+"F0.wireOp",EDGE,"E2.9.4.0")}),-1.0]])]});
            var Q59;
            Q59=makeQuery(id+"F0.imprint","IMPRINT",FACE,{"disambiguationData":[TD([[makeQuery(id+"F0.imprint","IMPRINT",EDGE,{"derivedFrom":sQuery(id+"F0.wireOp",EDGE,"E2.9.5.0")}),-1.0]])]});
            var Q60;
            Q60=makeQuery(id+"F0.imprint","IMPRINT",FACE,{"disambiguationData":[TD([[makeQuery(id+"F0.imprint","IMPRINT",EDGE,{"derivedFrom":sQuery(id+"F0.wireOp",EDGE,"E2.10.0.0")}),-1.0]])]});
            var Q61;
            Q61=makeQuery(id+"F0.imprint","IMPRINT",FACE,{"disambiguationData":[TD([[makeQuery(id+"F0.imprint","IMPRINT",EDGE,{"derivedFrom":sQuery(id+"F0.wireOp",EDGE,"E2.10.1.0")}),-1.0]])]});
            var Q62;
            Q62=makeQuery(id+"F0.imprint","IMPRINT",FACE,{"disambiguationData":[TD([[makeQuery(id+"F0.imprint","IMPRINT",EDGE,{"derivedFrom":sQuery(id+"F0.wireOp",EDGE,"E2.10.2.0")}),-1.0]])]});
            var Q63;
            Q63=makeQuery(id+"F0.imprint","IMPRINT",FACE,{"disambiguationData":[TD([[makeQuery(id+"F0.imprint","IMPRINT",EDGE,{"derivedFrom":sQuery(id+"F0.wireOp",EDGE,"E2.10.3.0")}),-1.0]])]});
            var Q64;
            Q64=makeQuery(id+"F0.imprint","IMPRINT",FACE,{"disambiguationData":[TD([[makeQuery(id+"F0.imprint","IMPRINT",EDGE,{"derivedFrom":sQuery(id+"F0.wireOp",EDGE,"E2.10.4.0")}),-1.0]])]});
            var Q65;
            Q65=makeQuery(id+"F0.imprint","IMPRINT",FACE,{"disambiguationData":[TD([[makeQuery(id+"F0.imprint","IMPRINT",EDGE,{"derivedFrom":sQuery(id+"F0.wireOp",EDGE,"E2.10.5.0")}),-1.0]])]});
            var Q66;
            Q66=makeQuery(id+"F0.imprint","IMPRINT",FACE,{"disambiguationData":[TD([[makeQuery(id+"F0.imprint","IMPRINT",EDGE,{"derivedFrom":sQuery(id+"F0.wireOp",EDGE,"E2.11.0.0")}),-1.0]])]});
            var Q67;
            Q67=makeQuery(id+"F0.imprint","IMPRINT",FACE,{"disambiguationData":[TD([[makeQuery(id+"F0.imprint","IMPRINT",EDGE,{"derivedFrom":sQuery(id+"F0.wireOp",EDGE,"E2.11.1.0")}),-1.0]])]});
            var Q68;
            Q68=makeQuery(id+"F0.imprint","IMPRINT",FACE,{"disambiguationData":[TD([[makeQuery(id+"F0.imprint","IMPRINT",EDGE,{"derivedFrom":sQuery(id+"F0.wireOp",EDGE,"E2.11.2.0")}),-1.0]])]});
            var Q69;
            Q69=makeQuery(id+"F0.imprint","IMPRINT",FACE,{"disambiguationData":[TD([[makeQuery(id+"F0.imprint","IMPRINT",EDGE,{"derivedFrom":sQuery(id+"F0.wireOp",EDGE,"E2.11.3.0")}),-1.0]])]});
            var Q70;
            Q70=makeQuery(id+"F0.imprint","IMPRINT",FACE,{"disambiguationData":[TD([[makeQuery(id+"F0.imprint","IMPRINT",EDGE,{"derivedFrom":sQuery(id+"F0.wireOp",EDGE,"E2.11.4.0")}),-1.0]])]});
            var Q71;
            Q71=makeQuery(id+"F0.imprint","IMPRINT",FACE,{"disambiguationData":[TD([[makeQuery(id+"F0.imprint","IMPRINT",EDGE,{"derivedFrom":sQuery(id+"F0.wireOp",EDGE,"E2.11.5.0")}),-1.0]])]});
            var Q72;
            Q72=makeQuery(id+"F0.imprint","IMPRINT",FACE,{"disambiguationData":[TD([[makeQuery(id+"F0.imprint","IMPRINT",EDGE,{"derivedFrom":sQuery(id+"F0.wireOp",EDGE,"E2.12.0.0")}),-1.0]])]});
            var Q73;
            Q73=makeQuery(id+"F0.imprint","IMPRINT",FACE,{"disambiguationData":[TD([[makeQuery(id+"F0.imprint","IMPRINT",EDGE,{"derivedFrom":sQuery(id+"F0.wireOp",EDGE,"E2.12.1.0")}),-1.0]])]});
            var Q74;
            Q74=makeQuery(id+"F0.imprint","IMPRINT",FACE,{"disambiguationData":[TD([[makeQuery(id+"F0.imprint","IMPRINT",EDGE,{"derivedFrom":sQuery(id+"F0.wireOp",EDGE,"E2.12.2.0")}),-1.0]])]});
            var Q75;
            Q75=makeQuery(id+"F0.imprint","IMPRINT",FACE,{"disambiguationData":[TD([[makeQuery(id+"F0.imprint","IMPRINT",EDGE,{"derivedFrom":sQuery(id+"F0.wireOp",EDGE,"E2.12.3.0")}),-1.0]])]});
            var Q76;
            Q76=makeQuery(id+"F0.imprint","IMPRINT",FACE,{"disambiguationData":[TD([[makeQuery(id+"F0.imprint","IMPRINT",EDGE,{"derivedFrom":sQuery(id+"F0.wireOp",EDGE,"E2.12.4.0")}),-1.0]])]});
            var Q77;
            Q77=makeQuery(id+"F0.imprint","IMPRINT",FACE,{"disambiguationData":[TD([[makeQuery(id+"F0.imprint","IMPRINT",EDGE,{"derivedFrom":sQuery(id+"F0.wireOp",EDGE,"E2.12.5.0")}),-1.0]])]});
            var Q78;
            Q78=makeQuery(id+"F0.imprint","IMPRINT",FACE,{"disambiguationData":[TD([[makeQuery(id+"F0.imprint","IMPRINT",EDGE,{"derivedFrom":sQuery(id+"F0.wireOp",EDGE,"E2.13.0.0")}),-1.0]])]});
            var Q79;
            Q79=makeQuery(id+"F0.imprint","IMPRINT",FACE,{"disambiguationData":[TD([[makeQuery(id+"F0.imprint","IMPRINT",EDGE,{"derivedFrom":sQuery(id+"F0.wireOp",EDGE,"E2.13.1.0")}),-1.0]])]});
            var Q80;
            Q80=makeQuery(id+"F0.imprint","IMPRINT",FACE,{"disambiguationData":[TD([[makeQuery(id+"F0.imprint","IMPRINT",EDGE,{"derivedFrom":sQuery(id+"F0.wireOp",EDGE,"E2.13.2.0")}),-1.0]])]});
            var Q81;
            Q81=makeQuery(id+"F0.imprint","IMPRINT",FACE,{"disambiguationData":[TD([[makeQuery(id+"F0.imprint","IMPRINT",EDGE,{"derivedFrom":sQuery(id+"F0.wireOp",EDGE,"E2.13.3.0")}),-1.0]])]});
            var Q82;
            Q82=makeQuery(id+"F0.imprint","IMPRINT",FACE,{"disambiguationData":[TD([[makeQuery(id+"F0.imprint","IMPRINT",EDGE,{"derivedFrom":sQuery(id+"F0.wireOp",EDGE,"E2.13.4.0")}),-1.0]])]});
            var Q83;
            Q83=makeQuery(id+"F0.imprint","IMPRINT",FACE,{"disambiguationData":[TD([[makeQuery(id+"F0.imprint","IMPRINT",EDGE,{"derivedFrom":sQuery(id+"F0.wireOp",EDGE,"E2.13.5.0")}),-1.0]])]});
            var Q84;
            Q84=makeQuery(id+"F0.imprint","IMPRINT",FACE,{"disambiguationData":[TD([[makeQuery(id+"F0.imprint","IMPRINT",EDGE,{"derivedFrom":sQuery(id+"F0.wireOp",EDGE,"E2.14.0.0")}),-1.0]])]});
            var Q85;
            Q85=makeQuery(id+"F0.imprint","IMPRINT",FACE,{"disambiguationData":[TD([[makeQuery(id+"F0.imprint","IMPRINT",EDGE,{"derivedFrom":sQuery(id+"F0.wireOp",EDGE,"E2.14.1.0")}),-1.0]])]});
            var Q86;
            Q86=makeQuery(id+"F0.imprint","IMPRINT",FACE,{"disambiguationData":[TD([[makeQuery(id+"F0.imprint","IMPRINT",EDGE,{"derivedFrom":sQuery(id+"F0.wireOp",EDGE,"E2.14.2.0")}),-1.0]])]});
            var Q87;
            Q87=makeQuery(id+"F0.imprint","IMPRINT",FACE,{"disambiguationData":[TD([[makeQuery(id+"F0.imprint","IMPRINT",EDGE,{"derivedFrom":sQuery(id+"F0.wireOp",EDGE,"E2.14.3.0")}),-1.0]])]});
            var Q88;
            Q88=makeQuery(id+"F0.imprint","IMPRINT",FACE,{"disambiguationData":[TD([[makeQuery(id+"F0.imprint","IMPRINT",EDGE,{"derivedFrom":sQuery(id+"F0.wireOp",EDGE,"E2.14.4.0")}),-1.0]])]});
            var Q89;
            Q89=makeQuery(id+"F0.imprint","IMPRINT",FACE,{"disambiguationData":[TD([[makeQuery(id+"F0.imprint","IMPRINT",EDGE,{"derivedFrom":sQuery(id+"F0.wireOp",EDGE,"E2.14.5.0")}),-1.0]])]});
            extrude(context, id + "F2", {"entities" : qUnion([Q0, Q1, Q2, Q3, Q4, Q5, Q6, Q7, Q8, Q9, Q10, Q11, Q12, Q13, Q14, Q15, Q16, Q17, Q18, Q19, Q20, Q21, Q22, Q23, Q24, Q25, Q26, Q27, Q28, Q29, Q30, Q31, Q32, Q33, Q34, Q35, Q36, Q37, Q38, Q39, Q40, Q41, Q42, Q43, Q44, Q45, Q46, Q47, Q48, Q49, Q50, Q51, Q52, Q53, Q54, Q55, Q56, Q57, Q58, Q59, Q60, Q61, Q62, Q63, Q64, Q65, Q66, Q67, Q68, Q69, Q70, Q71, Q72, Q73, Q74, Q75, Q76, Q77, Q78, Q79, Q80, Q81, Q82, Q83, Q84, Q85, Q86, Q87, Q88, Q89]), "operationType" : NewBodyOperationType.ADD, "depth" : 5 * mm});
        }
    });
